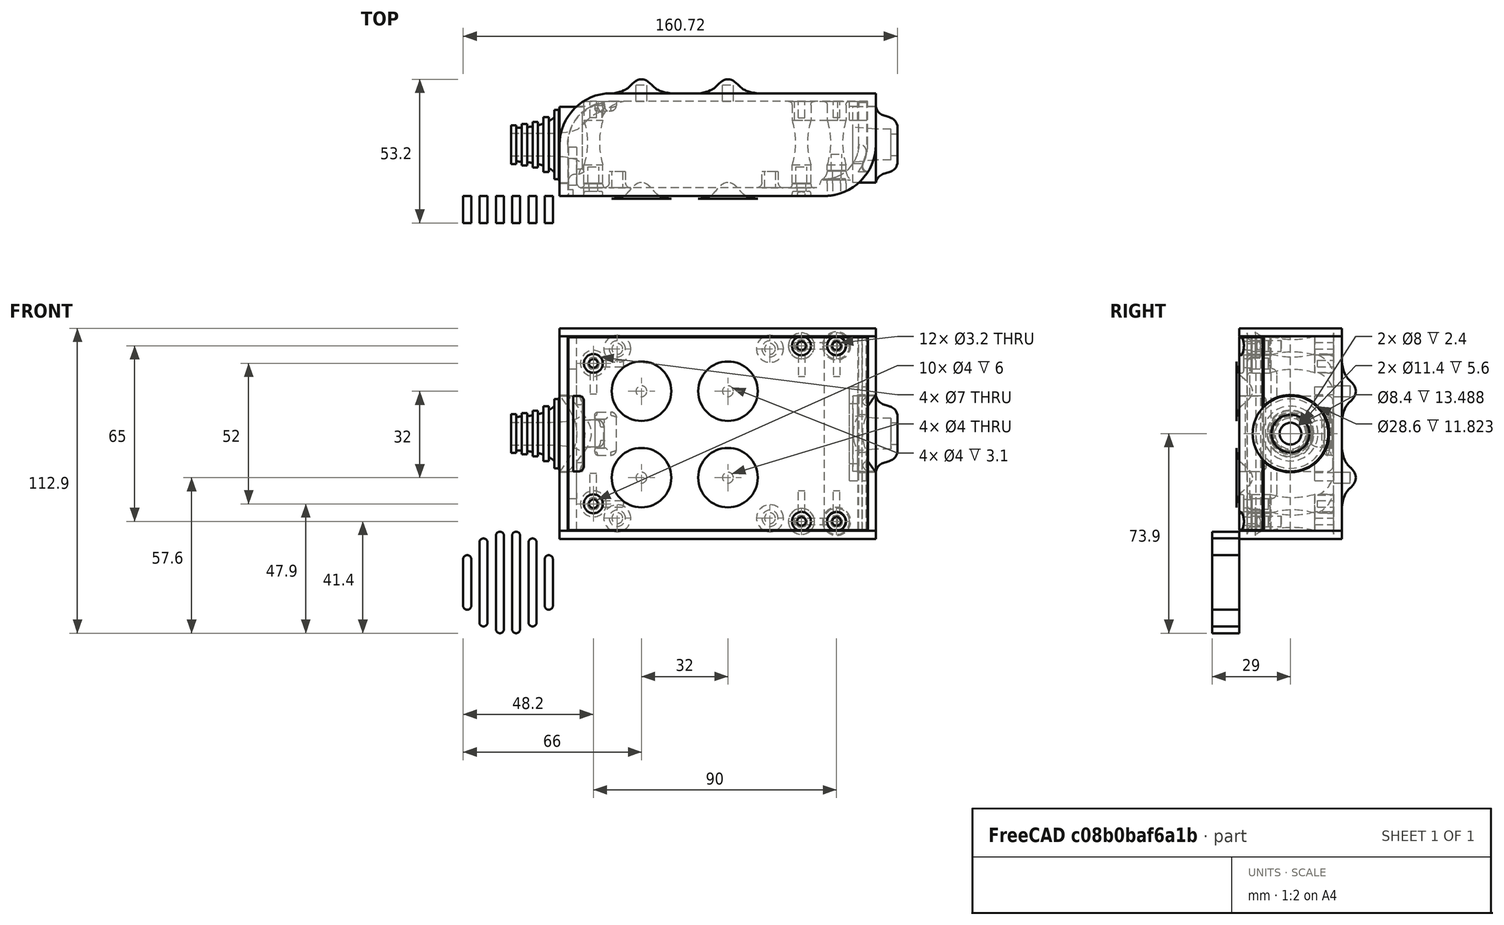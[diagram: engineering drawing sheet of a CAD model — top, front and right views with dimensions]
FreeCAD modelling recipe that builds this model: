
FCSTD DOCUMENT  (FreeCAD 0.19R0.19.2)
Label: enclosure_096
License: All rights reserved
LicenseURL: http://en.wikipedia.org/wiki/All_rights_reserved
objects: Part::Feature×72, Part::Revolution×72, Part::MultiFuse×52, Sketcher::SketchObject×29, Part::Fillet×22, Part::Cylinder×22, Part::Extrusion×19, Part::Cut×19, Part::Box×12, App::MeasureDistance×3
note: 319 computed .brp shape members not serialized (recipe doc carries the construction recipe); baked Part::Feature solids carry a one-line shape summary decoded from their .brp

FEATURE [Sketcher::SketchObject] Sketch  label="topSketch"
  FullyConstrained = true
  sketch-geometry (13):
    g0: LineSegment StartX=117 StartY=19 StartZ=0 EndX=117 EndY=38 EndZ=0
    g1: ArcOfCircle CenterX=98 CenterY=19 CenterZ=0 NormalX=0 NormalY=0 NormalZ=1 AngleXU=0 Radius=19 StartAngle=5.7297 EndAngle=6.28319
    g2: LineSegment StartX=0 StartY=3 StartZ=0 EndX=0 EndY=19 EndZ=0
    g3: LineSegment StartX=19 StartY=38 StartZ=0 EndX=117 EndY=38 EndZ=0
    g4: ArcOfCircle CenterX=19 CenterY=19 CenterZ=0 NormalX=0 NormalY=0 NormalZ=1 AngleXU=0 Radius=19 StartAngle=1.5708 EndAngle=3.14159
    g5: ArcOfCircle CenterX=19 CenterY=19 CenterZ=0 NormalX=0 NormalY=0 NormalZ=1 AngleXU=0 Radius=16 StartAngle=1.5708 EndAngle=3.14159
    g6: ArcOfCircle CenterX=98 CenterY=19 CenterZ=0 NormalX=0 NormalY=0 NormalZ=1 AngleXU=0 Radius=16 StartAngle=5.60905 EndAngle=6.28319
    g7: LineSegment StartX=114 StartY=19 StartZ=0 EndX=114 EndY=35 EndZ=0
    g8: LineSegment StartX=110.5 StartY=9.01251 StartZ=0 EndX=114.163 EndY=9.01251 EndZ=0
    g9: LineSegment StartX=114 StartY=35 StartZ=0 EndX=19 EndY=35 EndZ=0
    g10: LineSegment StartX=0 StartY=3 StartZ=0 EndX=0 EndY=0 EndZ=0
    g11: LineSegment StartX=3 StartY=0 StartZ=0 EndX=0 EndY=0 EndZ=0
    g12: LineSegment StartX=3 StartY=19 StartZ=0 EndX=3 EndY=0 EndZ=0
  constraints (33):
    c: Vertical(g0)
    c: Distance(g0) = 19
    c: Block(g0)
    c: Coincident(g1,g0)
    c: Block(g1)
    c: Vertical(g2)
    c: Block(g2)
    c: Coincident(g3,g0)
    c: Horizontal(g3)
    c: Distance(g3) = 98
    c: Coincident(g4,g3)
    c: Coincident(g4,g2)
    c: Block(g4)
    c: Coincident(g5,g4)
    c: Coincident(g6,g1)
    c: Block(g6)
    c: Block(g5)
    c: Coincident(g7,g6)
    c: Vertical(g7)
    c: Coincident(g8,g6)
    c: Coincident(g8,g1)
    c: Coincident(g9,g7)
    c: Coincident(g9,g5)
    c: Horizontal(g9)
    c: Tangent(g9,g5)
    c: Coincident(g10,g2)
    c: Distance(g10) = 3
    c: Vertical(g10)
    c: Coincident(g11,g10)
    c: Horizontal(g11)
    c: Coincident(g12,g5)
    c: Coincident(g12,g11)
    c: Vertical(g12)
FEATURE [Sketcher::SketchObject] Sketch001  label="bottomSketch"
  FullyConstrained = true
  sketch-geometry (32):
    g0: LineSegment StartX=3.3 StartY=-6.03275e-07 StartZ=0 EndX=98 EndY=-6.03275e-07 EndZ=0
    g1: ArcOfCircle CenterX=98 CenterY=19 CenterZ=0 NormalX=0 NormalY=0 NormalZ=1 AngleXU=0 Radius=19 StartAngle=4.71239 EndAngle=5.71103
    g2: LineSegment StartX=6.3 StartY=8 StartZ=0 EndX=3.3 EndY=8 EndZ=0
    g3: LineSegment StartX=3.3 StartY=8 StartZ=0 EndX=3.3 EndY=-6.03275e-07 EndZ=0
    g4: ArcOfCircle CenterX=8.3 CenterY=5 CenterZ=0 NormalX=0 NormalY=0 NormalZ=1 AngleXU=0 Radius=2 StartAngle=3.14159 EndAngle=4.71239
    g5: LineSegment StartX=6.3 StartY=8 StartZ=0 EndX=6.3 EndY=5 EndZ=0
    g6: ArcOfCircle CenterX=98 CenterY=19 CenterZ=0 NormalX=0 NormalY=0 NormalZ=1 AngleXU=0 Radius=12.7 StartAngle=4.71239 EndAngle=6.28319
    g7: LineSegment StartX=94.7 StartY=3 StartZ=0 EndX=8.3 EndY=3 EndZ=0
    g8-g12: Circle x5 (B-spline internal-alignment scaffolding for g13; pole/knot coordinates omitted)
    g13: BSplineCurve PolesCount=5 KnotsCount=3 Degree=3 IsPeriodic=0
    g14: GeomPoint X=98 Y=6.3 Z=0
    g15: GeomPoint X=96.3938 Y=4.71946 Z=0
    g16: GeomPoint X=94.7 Y=3 Z=0
    g17-g23: Circle x7 (B-spline internal-alignment scaffolding for g24; pole/knot coordinates omitted)
    g24: BSplineCurve PolesCount=7 KnotsCount=5 Degree=3 IsPeriodic=0
    g25-g29: GeomPoint x5 (B-spline internal-alignment scaffolding for g24; pole/knot coordinates omitted)
    g30: ArcOfCircle CenterX=98 CenterY=19 CenterZ=0 NormalX=0 NormalY=0 NormalZ=1 AngleXU=0 Radius=15.7 StartAngle=5.81226 EndAngle=6.28319
    g31: LineSegment StartX=110.7 StartY=19 StartZ=0 EndX=113.7 EndY=19 EndZ=0
  constraints (41):
    c: Horizontal(g0)
    c: Coincident(g1,g0)
    c: Block(g1)
    c: Horizontal(g2)
    c: Distance(g2) = 3
    c: Coincident(g3,g2)
    c: Vertical(g3)
    c: Coincident(g3,g0)
    c: Block(g4)
    c: Block(g2)
    c: Coincident(g5,g2)
    c: Coincident(g5,g4)
    c: Vertical(g5)
    c: Coincident(g6,g1)
    c: Block(g6)
    c: Coincident(g7,g4)
    c: Horizontal(g7)
    c: Block(g0)
    c: Block(g7)
    c: Block(g3)
    c: Coincident(g13,g6)
    c: Weight(g8) = 1
    c: Equal(g8, g9-g12) x4
    c: Coincident(g13,g7)
    c: InternalAlignment(g8-g12 -> g13) x5
    c: InternalAlignment(g14,g13)
    c: InternalAlignment(g15,g13)
    c: InternalAlignment(g16,g13)
    c: Block(g13)
    c: Weight(g17) = 1
    c: Equal(g17, g18-g23) x6
    c: Coincident(g24,g1)
    c: InternalAlignment(g17-g23 -> g24) x7
    c: InternalAlignment(g25-g29 -> g24) x5
    c: Block(g24)
    c: Coincident(g30,g24)
    c: Coincident(g31,g6)
    c: Coincident(g31,g30)
    c: Horizontal(g31)
    c: Block(g31)
    c: Block(g30)
FEATURE [Part::Extrusion] Extrude  label="top"
  Base = -> Sketch
  Dir = (0,0,1)
  DirMode = 2
  FaceMakerClass = Part::FaceMakerBullseye
  LengthFwd = 72
  LengthRev = 0
  Solid = true
  Symmetric = false
FEATURE [Part::Extrusion] Extrude001  label="bottom"
  Base = -> Sketch001
  Dir = (0,0,1)
  DirMode = 2
  FaceMakerClass = Part::FaceMakerBullseye
  LengthFwd = 71.4
  LengthRev = 0
  Placement = pos=(0,0,0.3) rot=(0,0,1;0rad)
  Solid = true
  Symmetric = false
FEATURE [Sketcher::SketchObject] Sketch002  label="topSketch001"
  FullyConstrained = true
  sketch-geometry (6):
    g0: LineSegment StartX=19 StartY=38 StartZ=0 EndX=117 EndY=38 EndZ=0
    g1: ArcOfCircle CenterX=19 CenterY=19 CenterZ=0 NormalX=0 NormalY=0 NormalZ=1 AngleXU=0 Radius=19 StartAngle=1.5708 EndAngle=3.14159
    g2: LineSegment StartX=117 StartY=38 StartZ=0 EndX=117 EndY=19 EndZ=0
    g3: LineSegment StartX=98 StartY=1.0161e-12 StartZ=0 EndX=5.22862e-06 EndY=1.0161e-12 EndZ=0
    g4: LineSegment StartX=5.22862e-06 StartY=19 StartZ=0 EndX=5.22862e-06 EndY=1.0161e-12 EndZ=0
    g5: ArcOfCircle CenterX=98 CenterY=19 CenterZ=0 NormalX=0 NormalY=0 NormalZ=1 AngleXU=0 Radius=19 StartAngle=4.71239 EndAngle=6.28319
  constraints (16):
    c: Horizontal(g0)
    c: Distance(g0) = 98
    c: Coincident(g1,g0)
    c: Block(g1)
    c: Coincident(g2,g0)
    c: Vertical(g2)
    c: Distance(g2) = 19
    c: Horizontal(g3)
    c: Coincident(g4,g1)
    c: Vertical(g4)
    c: Coincident(g3,g4)
    c: Block(g3)
    c: Coincident(g5,g2)
    c: Coincident(g5,g3)
    c: Block(g0)
    c: Block(g5)
FEATURE [Part::Extrusion] Extrude002  label="sideA"
  Base = -> Sketch002
  Dir = (0,0,1)
  DirMode = 2
  FaceMakerClass = Part::FaceMakerBullseye
  LengthFwd = 3
  LengthRev = 0
  Placement = pos=(0,0,-3) rot=(0,0,1;0rad)
  Solid = true
  Symmetric = false
FEATURE [Sketcher::SketchObject] Sketch003  label="topSketch002"
  FullyConstrained = true
  sketch-geometry (6):
    g0: LineSegment StartX=19 StartY=38 StartZ=0 EndX=117 EndY=38 EndZ=0
    g1: ArcOfCircle CenterX=19 CenterY=19 CenterZ=0 NormalX=0 NormalY=0 NormalZ=1 AngleXU=0 Radius=19 StartAngle=1.5708 EndAngle=3.14159
    g2: LineSegment StartX=117 StartY=38 StartZ=0 EndX=117 EndY=19 EndZ=0
    g3: LineSegment StartX=98 StartY=1.0161e-12 StartZ=0 EndX=5.22862e-06 EndY=1.0161e-12 EndZ=0
    g4: LineSegment StartX=5.22862e-06 StartY=19 StartZ=0 EndX=5.22862e-06 EndY=1.0161e-12 EndZ=0
    g5: ArcOfCircle CenterX=98 CenterY=19 CenterZ=0 NormalX=0 NormalY=0 NormalZ=1 AngleXU=0 Radius=19 StartAngle=4.71239 EndAngle=6.28319
  constraints (16):
    c: Horizontal(g0)
    c: Distance(g0) = 98
    c: Coincident(g1,g0)
    c: Block(g1)
    c: Coincident(g2,g0)
    c: Vertical(g2)
    c: Distance(g2) = 19
    c: Horizontal(g3)
    c: Coincident(g4,g1)
    c: Vertical(g4)
    c: Coincident(g3,g4)
    c: Block(g3)
    c: Coincident(g5,g2)
    c: Coincident(g5,g3)
    c: Block(g0)
    c: Block(g5)
FEATURE [Part::Extrusion] Extrude003  label="sideB"
  Base = -> Sketch003
  Dir = (0,0,1)
  DirMode = 2
  FaceMakerClass = Part::FaceMakerBullseye
  LengthFwd = 3
  LengthRev = 0
  Placement = pos=(0,0,72) rot=(0,0,1;0rad)
  Solid = true
  Symmetric = false
FEATURE [Sketcher::SketchObject] Sketch004
  FullyConstrained = true
  MapMode = 3
  Placement = pos=(0,0,0) rot=(1,0,0;1.5708rad)
  Support = -> [Extrude]
  sketch-geometry (8):
    g0: Circle CenterX=80.351 CenterY=-67.6202 CenterZ=0 NormalX=0 NormalY=0 NormalZ=1 AngleXU=0 Radius=2
    g1: Circle CenterX=80.351 CenterY=-67.6202 CenterZ=0 NormalX=0 NormalY=0 NormalZ=1 AngleXU=0 Radius=3
    g2: Circle CenterX=80.351 CenterY=-4.92017 CenterZ=0 NormalX=0 NormalY=0 NormalZ=1 AngleXU=0 Radius=2
    g3: Circle CenterX=80.351 CenterY=-4.92017 CenterZ=0 NormalX=0 NormalY=0 NormalZ=1 AngleXU=0 Radius=3
    g4: Circle CenterX=23.851 CenterY=-4.92017 CenterZ=0 NormalX=0 NormalY=0 NormalZ=1 AngleXU=0 Radius=2
    g5: Circle CenterX=23.851 CenterY=-4.92017 CenterZ=0 NormalX=0 NormalY=0 NormalZ=1 AngleXU=0 Radius=3
    g6: Circle CenterX=23.851 CenterY=-67.6202 CenterZ=0 NormalX=0 NormalY=0 NormalZ=1 AngleXU=0 Radius=2
    g7: Circle CenterX=23.851 CenterY=-67.6202 CenterZ=0 NormalX=0 NormalY=0 NormalZ=1 AngleXU=0 Radius=3
  constraints (8):
    c: Block(g3)
    c: Block(g2)
    c: Block(g1)
    c: Block(g0)
    c: Block(g6)
    c: Block(g7)
    c: Block(g4)
    c: Block(g5)
FEATURE [Part::Extrusion] Extrude004
  Base = -> Sketch004
  Dir = (0,-1,2e-16)
  DirMode = 2
  FaceMakerClass = Part::FaceMakerBullseye
  LengthFwd = 6
  LengthRev = 0
  Placement = pos=(0,9,0) rot=(0,0,1;0rad)
  Solid = true
  Symmetric = false
FEATURE [Sketcher::SketchObject] Sketch005
  FullyConstrained = true
  MapMode = 3
  Placement = pos=(0,0,0) rot=(1,0,0;1.5708rad)
  Support = -> [Extrude]
  sketch-geometry (8):
    g0: Circle CenterX=80.351 CenterY=-67.6202 CenterZ=0 NormalX=0 NormalY=0 NormalZ=1 AngleXU=0 Radius=3
    g1: Circle CenterX=80.351 CenterY=-4.92017 CenterZ=0 NormalX=0 NormalY=0 NormalZ=1 AngleXU=0 Radius=3
    g2: Circle CenterX=23.851 CenterY=-4.92017 CenterZ=0 NormalX=0 NormalY=0 NormalZ=1 AngleXU=0 Radius=3
    g3: Circle CenterX=23.851 CenterY=-67.6202 CenterZ=0 NormalX=0 NormalY=0 NormalZ=1 AngleXU=0 Radius=3
    g4: Circle CenterX=23.851 CenterY=-67.6202 CenterZ=0 NormalX=0 NormalY=0 NormalZ=1 AngleXU=0 Radius=5
    g5: Circle CenterX=80.351 CenterY=-67.6202 CenterZ=0 NormalX=0 NormalY=0 NormalZ=1 AngleXU=0 Radius=5
    g6: Circle CenterX=23.851 CenterY=-4.92017 CenterZ=0 NormalX=0 NormalY=0 NormalZ=1 AngleXU=0 Radius=5
    g7: Circle CenterX=80.351 CenterY=-4.92017 CenterZ=0 NormalX=0 NormalY=0 NormalZ=1 AngleXU=0 Radius=5
  constraints (8):
    c: Block(g1)
    c: Block(g0)
    c: Block(g3)
    c: Block(g2)
    c: Block(g5)
    c: Block(g4)
    c: Block(g6)
    c: Block(g7)
FEATURE [Part::Extrusion] Extrude005
  Base = -> Sketch005
  Dir = (0,-1,2e-16)
  DirMode = 2
  FaceMakerClass = Part::FaceMakerBullseye
  LengthFwd = 2
  LengthRev = 0
  Solid = true
  Symmetric = false
FEATURE [Sketcher::SketchObject] Sketch006
  FullyConstrained = true
  MapMode = 3
  Placement = pos=(0,0,0) rot=(1,0,0;1.5708rad)
  sketch-geometry (8):
    g0: Circle CenterX=80.351 CenterY=-67.6202 CenterZ=0 NormalX=0 NormalY=0 NormalZ=1 AngleXU=0 Radius=3
    g1: Circle CenterX=80.351 CenterY=-4.92017 CenterZ=0 NormalX=0 NormalY=0 NormalZ=1 AngleXU=0 Radius=3
    g2: Circle CenterX=23.851 CenterY=-4.92017 CenterZ=0 NormalX=0 NormalY=0 NormalZ=1 AngleXU=0 Radius=3
    g3: Circle CenterX=23.851 CenterY=-67.6202 CenterZ=0 NormalX=0 NormalY=0 NormalZ=1 AngleXU=0 Radius=3
    g4: Circle CenterX=23.851 CenterY=-67.6202 CenterZ=0 NormalX=0 NormalY=0 NormalZ=1 AngleXU=0 Radius=5
    g5: Circle CenterX=80.351 CenterY=-67.6202 CenterZ=0 NormalX=0 NormalY=0 NormalZ=1 AngleXU=0 Radius=5
    g6: Circle CenterX=23.851 CenterY=-4.92017 CenterZ=0 NormalX=0 NormalY=0 NormalZ=1 AngleXU=0 Radius=5
    g7: Circle CenterX=80.351 CenterY=-4.92017 CenterZ=0 NormalX=0 NormalY=0 NormalZ=1 AngleXU=0 Radius=5
  constraints (8):
    c: Block(g1)
    c: Block(g0)
    c: Block(g3)
    c: Block(g2)
    c: Block(g5)
    c: Block(g4)
    c: Block(g6)
    c: Block(g7)
FEATURE [Part::Extrusion] Extrude007
  Base = -> Sketch006
  Dir = (0,-1,2e-16)
  DirMode = 2
  FaceMakerClass = Part::FaceMakerBullseye
  LengthFwd = 2
  LengthRev = 0
  Solid = true
  Symmetric = false
FEATURE [Part::Fillet] Fillet
  Base = -> Extrude007
  Edges = 4 edges r=1.99: [Edge6,Edge12,Edge18,Edge24]
FEATURE [Part::Cut] Cut
  Base = -> Extrude005
  Placement = pos=(0,5,0) rot=(0,0,1;0rad)
  Tool = -> Fillet
FEATURE [Part::MultiFuse] Fusion  label="pCBScrews"
  Placement = pos=(-2.5,0,72.3) rot=(0,0,1;0rad)
  Shapes = -> [Extrude004,Cut]
FEATURE [App::MeasureDistance] Distance  label="Distance: 0.69 mm"
  Distance = 0.685967
  P1 = (24.0138,2.9647,0.3)
  P2 = (23.8901,3,-0.373787)
FEATURE [App::MeasureDistance] Distance001  label="Distance: 0.53 mm"
  Distance = 0.533607
  P1 = (80.2939,3,72.2334)
  P2 = (80.281,2.99661,71.7)
FEATURE [Part::Fillet] Fillet001
  Base = -> Extrude001
  Edges = 1 edges r=2.4: [Edge17]
FEATURE [Part::Fillet] Fillet002  label="bottom001"
  Base = -> Fillet001
  Edges = 1 edges r=2.4: [Edge36]
FEATURE [Part::Fillet] Fillet003  label="top001"
  Base = -> Extrude
  Edges = 1 edges r=2: [Edge1]
FEATURE [Sketcher::SketchObject] Sketch007
  FullyConstrained = true
  sketch-geometry (16):
    g0: LineSegment StartX=4 StartY=0 StartZ=0 EndX=4 EndY=2.4 EndZ=0
    g1: LineSegment StartX=4 StartY=2.4 StartZ=0 EndX=7 EndY=2.4 EndZ=0
    g2: LineSegment StartX=4 StartY=0 StartZ=0 EndX=5.7 EndY=0 EndZ=0
    g3: LineSegment StartX=5.7 StartY=0 StartZ=0 EndX=5.7 EndY=-5.6 EndZ=0
    g4-g8: Circle x5 (B-spline internal-alignment scaffolding for g9; pole/knot coordinates omitted)
    g9: BSplineCurve PolesCount=5 KnotsCount=3 Degree=3 IsPeriodic=0
    g10: GeomPoint X=7 Y=2.4 Z=0
    g11: GeomPoint X=10.4582 Y=-1.55472 Z=0
    g12: GeomPoint X=14 Y=-5.6 Z=0
    g13: LineSegment StartX=14 StartY=-5.6 StartZ=0 EndX=14 EndY=-14.1 EndZ=0
    g14: LineSegment StartX=14 StartY=-14.1 StartZ=0 EndX=6.5 EndY=-14.1 EndZ=0
    g15: LineSegment StartX=5.7 StartY=-5.6 StartZ=0 EndX=6.5 EndY=-14.1 EndZ=0
  constraints (28):
    c: Distance(g0) = 2.4
    c: Vertical(g0)
    c: Block(g0)
    c: Coincident(g1,g0)
    c: Horizontal(g1)
    c: Distance(g1) = 3
    c: Coincident(g2,g0)
    c: Horizontal(g2)
    c: Distance(g2) = 1.7
    c: Coincident(g3,g2)
    c: Vertical(g3)
    c: Distance(g3) = 5.6
    c: Coincident(g9,g1)
    c: Weight(g4) = 1
    c: Equal(g4, g5-g8) x4
    c: InternalAlignment(g4-g8 -> g9) x5
    c: InternalAlignment(g10,g9)
    c: InternalAlignment(g11,g9)
    c: InternalAlignment(g12,g9)
    c: Block(g9)
    c: Coincident(g13,g9)
    c: Vertical(g13)
    c: Distance(g13) = 8.5
    c: Coincident(g14,g13)
    c: Horizontal(g14)
    c: Distance(g14) = 7.5
    c: Coincident(g15,g3)
    c: Coincident(g15,g14)
FEATURE [Part::Feature] Face
  shape: bbox 10 x 16.5 x 2e-07 mm, 1 faces, 0 solids (baked)
FEATURE [Part::Revolution] Revolve  label="plugHousing"
  Angle = 360
  Axis = (0,1,0)
  Base = (0,0,0)
  FaceMakerClass = Part::FaceMakerBullseye
  Placement = pos=(0,0,36.15) rot=(0,0,1;0rad)
  Solid = false
  Source = -> Face
  Symmetric = false
FEATURE [Part::Feature] Face001
  shape: bbox 10 x 16.5 x 2e-07 mm, 1 faces, 0 solids (baked)
FEATURE [Part::Revolution] Revolve001  label="plugHousing001"
  Angle = 360
  Axis = (0,1,0)
  Base = (0,0,0)
  FaceMakerClass = Part::FaceMakerBullseye
  Placement = pos=(0,0,36.15) rot=(0,0,1;0rad)
  Solid = false
  Source = -> Face001
  Symmetric = false
FEATURE [Part::MultiFuse] Fusion001  label="plugHousing002"
  Placement = pos=(0,0,0) rot=(0,0,1;1.5708rad)
  Shapes = -> [Revolve001,Revolve]
FEATURE [Part::Feature] Face002
  shape: bbox 10 x 16.5 x 2e-07 mm, 1 faces, 0 solids (baked)
FEATURE [Part::Revolution] Revolve003  label="plugHousing005"
  Angle = 360
  Axis = (0,1,0)
  Base = (0,0,0)
  FaceMakerClass = Part::FaceMakerBullseye
  Placement = pos=(0,0,36.15) rot=(0,0,1;0rad)
  Solid = false
  Source = -> Face002
  Symmetric = false
FEATURE [Part::Feature] Face003
  shape: bbox 10 x 16.5 x 2e-07 mm, 1 faces, 0 solids (baked)
FEATURE [Part::Revolution] Revolve002  label="plugHousing003"
  Angle = 360
  Axis = (0,1,0)
  Base = (0,0,0)
  FaceMakerClass = Part::FaceMakerBullseye
  Placement = pos=(0,0,36.15) rot=(0,0,1;0rad)
  Solid = false
  Source = -> Face003
  Symmetric = false
FEATURE [Part::MultiFuse] Fusion002  label="plugHousing004"
  Placement = pos=(0,0,0) rot=(0,0,1;1.5708rad)
  Shapes = -> [Revolve002,Revolve003]
FEATURE [Part::MultiFuse] Fusion003  label="plugHousing006"
  Placement = pos=(0,19,0) rot=(0,0,1;3.14159rad)
  Shapes = -> [Fusion002,Fusion001]
FEATURE [Part::Feature] Face004
  shape: bbox 10 x 16.5 x 2e-07 mm, 1 faces, 0 solids (baked)
FEATURE [Part::Revolution] Revolve006  label="plugHousing010"
  Angle = 360
  Axis = (0,1,0)
  Base = (0,0,0)
  FaceMakerClass = Part::FaceMakerBullseye
  Placement = pos=(0,0,36.15) rot=(0,0,1;0rad)
  Solid = false
  Source = -> Face004
  Symmetric = false
FEATURE [Part::Feature] Face005
  shape: bbox 10 x 16.5 x 2e-07 mm, 1 faces, 0 solids (baked)
FEATURE [Part::Revolution] Revolve007  label="plugHousing011"
  Angle = 360
  Axis = (0,1,0)
  Base = (0,0,0)
  FaceMakerClass = Part::FaceMakerBullseye
  Placement = pos=(0,0,36.15) rot=(0,0,1;0rad)
  Solid = false
  Source = -> Face005
  Symmetric = false
FEATURE [Part::Feature] Face006
  shape: bbox 10 x 16.5 x 2e-07 mm, 1 faces, 0 solids (baked)
FEATURE [Part::Revolution] Revolve004  label="plugHousing007"
  Angle = 360
  Axis = (0,1,0)
  Base = (0,0,0)
  FaceMakerClass = Part::FaceMakerBullseye
  Placement = pos=(0,0,36.15) rot=(0,0,1;0rad)
  Solid = false
  Source = -> Face006
  Symmetric = false
FEATURE [Part::MultiFuse] Fusion004  label="plugHousing009"
  Placement = pos=(0,0,0) rot=(0,0,1;1.5708rad)
  Shapes = -> [Revolve004,Revolve007]
FEATURE [Part::Feature] Face007
  shape: bbox 10 x 16.5 x 2e-07 mm, 1 faces, 0 solids (baked)
FEATURE [Part::Revolution] Revolve005  label="plugHousing008"
  Angle = 360
  Axis = (0,1,0)
  Base = (0,0,0)
  FaceMakerClass = Part::FaceMakerBullseye
  Placement = pos=(0,0,36.15) rot=(0,0,1;0rad)
  Solid = false
  Source = -> Face007
  Symmetric = false
FEATURE [Part::MultiFuse] Fusion005  label="plugHousing012"
  Placement = pos=(0,0,0) rot=(0,0,1;1.5708rad)
  Shapes = -> [Revolve006,Revolve005]
FEATURE [Part::MultiFuse] Fusion006  label="plugHousing013"
  Placement = pos=(0,19,0) rot=(0,0,1;3.14159rad)
  Shapes = -> [Fusion005,Fusion004]
FEATURE [Part::MultiFuse] Fusion007  label="plugHousing014"
  Placement = pos=(122.621,0,-0.15) rot=(0,0,1;0rad)
  Shapes = -> [Fusion003,Fusion006]
FEATURE [Part::Cylinder] Cylinder002
  Angle = 360
  AttacherType = Attacher::AttachEngine3D
  Height = 20
  Placement = pos=(0,0,36.15) rot=(0,0,1;0rad)
  Radius = 4
FEATURE [Part::Cylinder] Cylinder003
  Angle = 360
  AttacherType = Attacher::AttachEngine3D
  Height = 10
  Placement = pos=(0,0,36.15) rot=(0,0,1;0rad)
  Radius = 4
FEATURE [Part::MultiFuse] Fusion009  label="removeToCreateHoleForPlugHousing"
  Placement = pos=(70,19,36.15) rot=(0,1,0;1.5708rad)
  Shapes = -> [Cylinder002,Cylinder003]
FEATURE [Part::Cylinder] Cylinder004
  Angle = 360
  AttacherType = Attacher::AttachEngine3D
  Height = 20
  Placement = pos=(0,0,36.15) rot=(0,0,1;0rad)
  Radius = 4
FEATURE [Part::Cylinder] Cylinder005
  Angle = 360
  AttacherType = Attacher::AttachEngine3D
  Height = 10
  Placement = pos=(0,0,36.15) rot=(0,0,1;0rad)
  Radius = 4
FEATURE [Part::MultiFuse] Fusion010  label="removeToCreateHoleForPlugHousing001"
  Placement = pos=(70,19,36.15) rot=(0,1,0;1.5708rad)
  Shapes = -> [Cylinder004,Cylinder005]
FEATURE [Part::Cut] Cut001
  Base = -> Fillet003
  Tool = -> Fusion010
FEATURE [Part::Cut] Cut002  label="Bottom"
  Base = -> Fillet002
  Tool = -> Fusion009
FEATURE [Part::Feature] Face008
  shape: bbox 10 x 16.5 x 2e-07 mm, 1 faces, 0 solids (baked)
FEATURE [Part::Revolution] Revolve011  label="plugHousing021"
  Angle = 360
  Axis = (0,1,0)
  Base = (0,0,0)
  FaceMakerClass = Part::FaceMakerBullseye
  Placement = pos=(0,0,36.15) rot=(0,0,1;0rad)
  Solid = false
  Source = -> Face008
  Symmetric = false
FEATURE [Part::Feature] Face009
  shape: bbox 10 x 16.5 x 2e-07 mm, 1 faces, 0 solids (baked)
FEATURE [Part::Revolution] Revolve012  label="plugHousing022"
  Angle = 360
  Axis = (0,1,0)
  Base = (0,0,0)
  FaceMakerClass = Part::FaceMakerBullseye
  Placement = pos=(0,0,36.15) rot=(0,0,1;0rad)
  Solid = false
  Source = -> Face009
  Symmetric = false
FEATURE [Part::Feature] Face010 .. Face013  x4 (patterned run collapsed; names and placements below)
  shape: bbox 10 x 16.5 x 2e-07 mm, 1 faces, 0 solids (baked)
FEATURE [Part::Revolution] Revolve015  label="plugHousing027"
  Angle = 360
  Axis = (0,1,0)
  Base = (0,0,0)
  FaceMakerClass = Part::FaceMakerBullseye
  Placement = pos=(0,0,36.15) rot=(0,0,1;0rad)
  Solid = false
  Source = -> Face013
  Symmetric = false
FEATURE [Part::Feature] Face014
  shape: bbox 10 x 16.5 x 2e-07 mm, 1 faces, 0 solids (baked)
FEATURE [Part::Feature] Face015
  shape: bbox 10 x 16.5 x 2e-07 mm, 1 faces, 0 solids (baked)
FEATURE [Part::Feature] Face016
  shape: bbox 10 x 16.5 x 2e-07 mm, 1 faces, 0 solids (baked)
FEATURE [Part::Revolution] Revolve019  label="plugHousing033"
  Angle = 360
  Axis = (0,1,0)
  Base = (0,0,0)
  FaceMakerClass = Part::FaceMakerBullseye
  Placement = pos=(0,0,36.15) rot=(0,0,1;0rad)
  Solid = false
  Source = -> Face016
  Symmetric = false
FEATURE [Part::Feature] Face017
  shape: bbox 10 x 16.5 x 2e-07 mm, 1 faces, 0 solids (baked)
FEATURE [Part::Revolution] Revolve020  label="plugHousing034"
  Angle = 360
  Axis = (0,1,0)
  Base = (0,0,0)
  FaceMakerClass = Part::FaceMakerBullseye
  Placement = pos=(0,0,36.15) rot=(0,0,1;0rad)
  Solid = false
  Source = -> Face017
  Symmetric = false
FEATURE [Part::Feature] Face018
  shape: bbox 10 x 16.5 x 2e-07 mm, 1 faces, 0 solids (baked)
FEATURE [Part::Revolution] Revolve016  label="plugHousing030"
  Angle = 360
  Axis = (0,1,0)
  Base = (0,0,0)
  FaceMakerClass = Part::FaceMakerBullseye
  Placement = pos=(0,0,36.15) rot=(0,0,1;0rad)
  Solid = false
  Source = -> Face018
  Symmetric = false
FEATURE [Part::MultiFuse] Fusion020  label="plugHousing038"
  Placement = pos=(0,0,0) rot=(0,0,1;1.5708rad)
  Shapes = -> [Revolve016,Revolve020]
FEATURE [Part::Feature] Face019
  shape: bbox 10 x 16.5 x 2e-07 mm, 1 faces, 0 solids (baked)
FEATURE [Part::Feature] Face020
  shape: bbox 10 x 16.5 x 2e-07 mm, 1 faces, 0 solids (baked)
FEATURE [Part::Revolution] Revolve017  label="plugHousing031"
  Angle = 360
  Axis = (0,1,0)
  Base = (0,0,0)
  FaceMakerClass = Part::FaceMakerBullseye
  Placement = pos=(0,0,36.15) rot=(0,0,1;0rad)
  Solid = false
  Source = -> Face020
  Symmetric = false
FEATURE [Part::MultiFuse] Fusion021  label="plugHousing039"
  Placement = pos=(0,0,0) rot=(0,0,1;1.5708rad)
  Shapes = -> [Revolve019,Revolve017]
FEATURE [Part::MultiFuse] Fusion023  label="plugHousing041"
  Placement = pos=(0,19,0) rot=(0,0,1;3.14159rad)
  Shapes = -> [Fusion021,Fusion020]
FEATURE [Part::Revolution] Revolve022  label="plugHousing043"
  Angle = 360
  Axis = (0,1,0)
  Base = (0,0,0)
  FaceMakerClass = Part::FaceMakerBullseye
  Placement = pos=(0,0,36.15) rot=(0,0,1;0rad)
  Solid = false
  Source = -> Face019
  Symmetric = false
FEATURE [Part::Feature] Face021
  shape: bbox 10 x 16.5 x 2e-07 mm, 1 faces, 0 solids (baked)
FEATURE [Part::Revolution] Revolve023  label="plugHousing044"
  Angle = 360
  Axis = (0,1,0)
  Base = (0,0,0)
  FaceMakerClass = Part::FaceMakerBullseye
  Placement = pos=(0,0,36.15) rot=(0,0,1;0rad)
  Solid = false
  Source = -> Face021
  Symmetric = false
FEATURE [Part::Feature] Face022
  shape: bbox 10 x 16.5 x 2e-07 mm, 1 faces, 0 solids (baked)
FEATURE [Part::Revolution] Revolve018  label="plugHousing032"
  Angle = 360
  Axis = (0,1,0)
  Base = (0,0,0)
  FaceMakerClass = Part::FaceMakerBullseye
  Placement = pos=(0,0,36.15) rot=(0,0,1;0rad)
  Solid = false
  Source = -> Face022
  Symmetric = false
FEATURE [Part::MultiFuse] Fusion022  label="plugHousing040"
  Placement = pos=(0,0,0) rot=(0,0,1;1.5708rad)
  Shapes = -> [Revolve018,Revolve023]
FEATURE [Part::Feature] Face023
  shape: bbox 10 x 16.5 x 2e-07 mm, 1 faces, 0 solids (baked)
FEATURE [Part::Revolution] Revolve021  label="plugHousing035"
  Angle = 360
  Axis = (0,1,0)
  Base = (0,0,0)
  FaceMakerClass = Part::FaceMakerBullseye
  Placement = pos=(0,0,36.15) rot=(0,0,1;0rad)
  Solid = false
  Source = -> Face023
  Symmetric = false
FEATURE [Part::MultiFuse] Fusion018  label="plugHousing036"
  Placement = pos=(0,0,0) rot=(0,0,1;1.5708rad)
  Shapes = -> [Revolve022,Revolve021]
FEATURE [Part::MultiFuse] Fusion019  label="plugHousing037"
  Placement = pos=(0,19,0) rot=(0,0,1;3.14159rad)
  Shapes = -> [Fusion018,Fusion022]
FEATURE [Part::MultiFuse] Fusion024  label="plugHousing042"
  Placement = pos=(122.621,0,-0.15) rot=(0,0,1;0rad)
  Shapes = -> [Fusion023,Fusion019]
FEATURE [Part::Cylinder] Cylinder006
  Angle = 360
  AttacherType = Attacher::AttachEngine3D
  Height = 20
  Placement = pos=(0,0,36.15) rot=(0,0,1;0rad)
  Radius = 14.3
FEATURE [Part::Cylinder] Cylinder007
  Angle = 360
  AttacherType = Attacher::AttachEngine3D
  Height = 10
  Placement = pos=(0,0,36.15) rot=(0,0,1;0rad)
  Radius = 4
FEATURE [Part::MultiFuse] Fusion026  label="removeToCreteHoleForPlugHousing"
  Placement = pos=(70,19,36) rot=(0,1,0;1.5708rad)
  Shapes = -> [Cylinder006,Cylinder007]
FEATURE [Part::Box] Box001  label="Cube001"
  AttacherType = Attacher::AttachEngine3D
  Height = 28
  Length = 3
  Placement = pos=(110.7,19,22) rot=(0,0,1;0rad)
  Width = 15.7
FEATURE [Part::Cut] Cut003  label="top002"
  Base = -> Cut001
  Tool = -> Fusion007
FEATURE [Part::Revolution] Revolve008  label="plugHousing015"
  Angle = 360
  Axis = (0,1,0)
  Base = (0,0,0)
  FaceMakerClass = Part::FaceMakerBullseye
  Placement = pos=(0,0,36.15) rot=(0,0,1;0rad)
  Solid = false
  Source = -> Face010
  Symmetric = false
FEATURE [Part::MultiFuse] Fusion013  label="plugHousing020"
  Placement = pos=(0,0,0) rot=(0,0,1;1.5708rad)
  Shapes = -> [Revolve008,Revolve012]
FEATURE [Part::Cut] Cut004  label="top003"
  Base = -> Cut003
  Placement = pos=(1,0,0) rot=(0,0,1;0rad)
  Tool = -> Fusion026
FEATURE [Part::Cylinder] Cylinder008
  Angle = 360
  AttacherType = Attacher::AttachEngine3D
  Height = 20
  Placement = pos=(0,0,36.15) rot=(0,0,1;0rad)
  Radius = 10.3
FEATURE [Part::Cylinder] Cylinder009
  Angle = 360
  AttacherType = Attacher::AttachEngine3D
  Height = 10
  Placement = pos=(0,0,36.15) rot=(0,0,1;0rad)
  Radius = 4
FEATURE [Part::MultiFuse] Fusion027  label="removeToCreteHoleForPlugHousing001"
  Placement = pos=(70,19,36) rot=(0,1,0;1.5708rad)
  Shapes = -> [Cylinder008,Cylinder009]
FEATURE [Part::Cut] Cut005  label="plugHousingTab"
  Base = -> Box001
  Tool = -> Fusion027
FEATURE [Part::MultiFuse] Fusion028  label="plugHousing045"
  Shapes = -> [Fusion024,Cut005]
FEATURE [Part::Box] Box002  label="Cube002"
  AttacherType = Attacher::AttachEngine3D
  Height = 28.8
  Length = 3
  Placement = pos=(107.3,28,21.6) rot=(0,0,1;0rad)
  Width = 7
FEATURE [Part::Box] Box003  label="Cube003"
  AttacherType = Attacher::AttachEngine3D
  Height = 3
  Length = 6.4
  Placement = pos=(107.3,28,18.6) rot=(0,0,1;0rad)
  Width = 7
FEATURE [Part::Box] Box004  label="Cube004"
  AttacherType = Attacher::AttachEngine3D
  Height = 3
  Length = 6.4
  Placement = pos=(107.3,28,50.4) rot=(0,0,1;0rad)
  Width = 7
FEATURE [Part::MultiFuse] Fusion029  label="plugHousingBracketHolder"
  Shapes = -> [Box004,Box002,Box003]
FEATURE [Part::Cylinder] Cylinder010
  Angle = 360
  AttacherType = Attacher::AttachEngine3D
  Height = 20
  Placement = pos=(0,0,36.15) rot=(0,0,1;0rad)
  Radius = 14.3
FEATURE [Part::Cylinder] Cylinder011
  Angle = 360
  AttacherType = Attacher::AttachEngine3D
  Height = 10
  Placement = pos=(0,0,36.15) rot=(0,0,1;0rad)
  Radius = 4
FEATURE [Part::MultiFuse] Fusion030  label="removeToCreteHoleForPlugHousing002"
  Placement = pos=(70,19,36) rot=(0,1,0;1.5708rad)
  Shapes = -> [Cylinder010,Cylinder011]
FEATURE [Part::Cut] Cut006  label="plugHousingBracketHolder001"
  Base = -> Fusion029
  Tool = -> Fusion030
FEATURE [Part::Cylinder] Cylinder012
  Angle = 360
  AttacherType = Attacher::AttachEngine3D
  Height = 20
  Placement = pos=(0,0,36.15) rot=(0,0,1;0rad)
  Radius = 7
FEATURE [Part::Cylinder] Cylinder013
  Angle = 360
  AttacherType = Attacher::AttachEngine3D
  Height = 10
  Placement = pos=(0,0,36.15) rot=(0,0,1;0rad)
  Radius = 4
FEATURE [Part::MultiFuse] Fusion032  label="removeToCreteHoleForPlugHousing003"
  Placement = pos=(70,19,36) rot=(0,1,0;1.5708rad)
  Shapes = -> [Cylinder012,Cylinder013]
FEATURE [Part::Cut] Cut007  label="bottom002"
  Base = -> Cut002
  Tool = -> Fusion032
FEATURE [Sketcher::SketchObject] Sketch008
  FullyConstrained = true
  sketch-geometry (54):
    g0: LineSegment StartX=-4.2 StartY=0 StartZ=0 EndX=-6.2 EndY=0 EndZ=0
    g1: LineSegment StartX=-14 StartY=-18 StartZ=0 EndX=-14 EndY=-26.5 EndZ=0
    g2: LineSegment StartX=-4.2 StartY=0 StartZ=0 EndX=-4.2 EndY=-13.4877 EndZ=0
    g3: Circle CenterX=-4.2 CenterY=-13.4877 CenterZ=0 NormalX=0 NormalY=0 NormalZ=1 AngleXU=0 Radius=1
    g4: Circle CenterX=-4.2 CenterY=-26.5 CenterZ=0 NormalX=0 NormalY=0 NormalZ=1 AngleXU=0 Radius=1
    g5: Circle CenterX=-8.2 CenterY=-26.5 CenterZ=0 NormalX=0 NormalY=0 NormalZ=1 AngleXU=0 Radius=1
    g6: BSplineCurve PolesCount=3 KnotsCount=2 Degree=2 IsPeriodic=0
    g7: GeomPoint X=-4.2 Y=-13.4877 Z=0
    g8: GeomPoint X=-8.2 Y=-26.5 Z=0
    g9: LineSegment StartX=-14 StartY=-26.5 StartZ=0 EndX=-8.2 EndY=-26.5 EndZ=0
    g10: LineSegment StartX=-10.15 StartY=-12 StartZ=0 EndX=-10.15 EndY=-14 EndZ=0
    g11: LineSegment StartX=-12.8401 StartY=-16 StartZ=0 EndX=-10.1571 EndY=-16 EndZ=0
    g12: LineSegment StartX=-10.15 StartY=-14 StartZ=0 EndX=-8.70761 EndY=-14 EndZ=0
    g13: LineSegment StartX=-12.8401 StartY=-16 StartZ=0 EndX=-12.8401 EndY=-17.6958 EndZ=0
    g14: LineSegment StartX=-10.15 StartY=-12 StartZ=0 EndX=-7.79258 EndY=-12 EndZ=0
    g15: Circle CenterX=-6.2215 CenterY=-2 CenterZ=0 NormalX=0 NormalY=0 NormalZ=1 AngleXU=0 Radius=1
    g16: Circle CenterX=-6.22762 CenterY=-2.58724 CenterZ=0 NormalX=0 NormalY=0 NormalZ=1 AngleXU=0 Radius=1
    g17: Circle CenterX=-6.32538 CenterY=-4 CenterZ=0 NormalX=0 NormalY=0 NormalZ=1 AngleXU=0 Radius=1
    g18: BSplineCurve PolesCount=3 KnotsCount=2 Degree=2 IsPeriodic=0
    g19: GeomPoint X=-6.2215 Y=-2 Z=0
    g20: GeomPoint X=-6.32538 Y=-4 Z=0
    g21: Circle CenterX=-6.48644 CenterY=-5.99526 CenterZ=0 NormalX=0 NormalY=0 NormalZ=1 AngleXU=0 Radius=1
    g22: Circle CenterX=-6.58486 CenterY=-6.99526 CenterZ=0 NormalX=0 NormalY=0 NormalZ=1 AngleXU=0 Radius=1
    g23: Circle CenterX=-6.77343 CenterY=-8 CenterZ=0 NormalX=0 NormalY=0 NormalZ=1 AngleXU=0 Radius=1
    g24: BSplineCurve PolesCount=3 KnotsCount=2 Degree=2 IsPeriodic=0
    g25: GeomPoint X=-6.48644 Y=-5.99526 Z=0
    g26: GeomPoint X=-6.77343 Y=-8 Z=0
    g27: Circle CenterX=-7.19003 CenterY=-10 CenterZ=0 NormalX=0 NormalY=0 NormalZ=1 AngleXU=0 Radius=1
    g28: Circle CenterX=-7.44407 CenterY=-11.0915 CenterZ=0 NormalX=0 NormalY=0 NormalZ=1 AngleXU=0 Radius=1
    g29: Circle CenterX=-7.79258 CenterY=-12 CenterZ=0 NormalX=0 NormalY=0 NormalZ=1 AngleXU=0 Radius=1
    g30: BSplineCurve PolesCount=3 KnotsCount=2 Degree=2 IsPeriodic=0
    g31: GeomPoint X=-7.19003 Y=-10 Z=0
    g32: GeomPoint X=-7.79258 Y=-12 Z=0
    g33: Circle CenterX=-8.70761 CenterY=-14 CenterZ=0 NormalX=0 NormalY=0 NormalZ=1 AngleXU=0 Radius=1
    g34: Circle CenterX=-9.33087 CenterY=-15.1837 CenterZ=0 NormalX=0 NormalY=0 NormalZ=1 AngleXU=0 Radius=1
    g35: Circle CenterX=-10.1571 CenterY=-16 CenterZ=0 NormalX=0 NormalY=0 NormalZ=1 AngleXU=0 Radius=1
    g36: BSplineCurve PolesCount=3 KnotsCount=2 Degree=2 IsPeriodic=0
    g37: GeomPoint X=-8.70761 Y=-14 Z=0
    g38: GeomPoint X=-10.1571 Y=-16 Z=0
    g39: Circle CenterX=-12.8401 CenterY=-17.6958 CenterZ=0 NormalX=0 NormalY=0 NormalZ=1 AngleXU=0 Radius=1
    g40: Circle CenterX=-13.3521 CenterY=-17.9027 CenterZ=0 NormalX=0 NormalY=0 NormalZ=1 AngleXU=0 Radius=1
    g41: Circle CenterX=-14 CenterY=-18 CenterZ=0 NormalX=0 NormalY=0 NormalZ=1 AngleXU=0 Radius=1
    g42: BSplineCurve PolesCount=3 KnotsCount=2 Degree=2 IsPeriodic=0
    g43: GeomPoint X=-12.8401 Y=-17.6958 Z=0
    g44: GeomPoint X=-14 Y=-18 Z=0
    g45: LineSegment StartX=-6.2 StartY=0 StartZ=0 EndX=-7.2 EndY=0 EndZ=0
    g46: LineSegment StartX=-7.2 StartY=0 StartZ=0 EndX=-7.2 EndY=-2 EndZ=0
    g47: LineSegment StartX=-7.2 StartY=-2 StartZ=0 EndX=-6.2215 EndY=-2 EndZ=0
    g48: LineSegment StartX=-6.32538 StartY=-4 StartZ=0 EndX=-7.65538 EndY=-4 EndZ=0
    g49: LineSegment StartX=-7.65538 StartY=-4 StartZ=0 EndX=-7.65538 EndY=-5.99526 EndZ=0
    g50: LineSegment StartX=-7.65538 StartY=-5.99526 StartZ=0 EndX=-6.48644 EndY=-5.99526 EndZ=0
    g51: LineSegment StartX=-6.77343 StartY=-8 StartZ=0 EndX=-8.43343 EndY=-8 EndZ=0
    g52: LineSegment StartX=-8.43343 StartY=-8 StartZ=0 EndX=-8.43343 EndY=-10 EndZ=0
    g53: LineSegment StartX=-8.43343 StartY=-10 StartZ=0 EndX=-7.19003 EndY=-10 EndZ=0
  constraints (112):
    c: Horizontal(g0)
    c: Distance(g0) = 2
    c: Block(g0)
    c: Vertical(g1)
    c: Coincident(g2,g0)
    c: Vertical(g2)
    c: Block(g2)
    c: Coincident(g6,g2)
    c: Weight(g3) = 1
    c: Equal(g3,g4)
    c: Equal(g3,g5)
    c: InternalAlignment(g3,g6)
    c: InternalAlignment(g4,g6)
    c: InternalAlignment(g5,g6)
    c: InternalAlignment(g7,g6)
    c: InternalAlignment(g8,g6)
    c: Block(g6)
    c: Coincident(g9,g1)
    c: Coincident(g9,g6)
    c: Horizontal(g9)
    c: Vertical(g10)
    c: Block(g10)
    c: Horizontal(g11)
    c: Block(g11)
    c: Coincident(g12,g10)
    c: Horizontal(g12)
    c: Block(g12)
    c: Coincident(g13,g11)
    c: Vertical(g13)
    c: Block(g13)
    c: Coincident(g14,g10)
    c: Horizontal(g14)
    c: Block(g14)
    c: Block(g9)
    c: Block(g1)
    c: Weight(g15) = 1
    c: Equal(g15,g16)
    c: Equal(g15,g17)
    c: InternalAlignment(g15,g18)
    c: InternalAlignment(g16,g18)
    c: InternalAlignment(g17,g18)
    c: InternalAlignment(g19,g18)
    c: InternalAlignment(g20,g18)
    c: Weight(g21) = 1
    c: Equal(g21,g22)
    c: Equal(g21,g23)
    c: InternalAlignment(g21,g24)
    c: InternalAlignment(g22,g24)
    c: InternalAlignment(g23,g24)
    c: InternalAlignment(g25,g24)
    c: InternalAlignment(g26,g24)
    c: Weight(g27) = 1
    c: Equal(g27,g28)
    c: Equal(g27,g29)
    c: Coincident(g30,g14)
    c: InternalAlignment(g27,g30)
    c: InternalAlignment(g28,g30)
    c: InternalAlignment(g29,g30)
    c: InternalAlignment(g31,g30)
    c: InternalAlignment(g32,g30)
    c: Coincident(g36,g12)
    c: Weight(g33) = 1
    c: Equal(g33,g34)
    c: Equal(g33,g35)
    c: Coincident(g36,g11)
    c: InternalAlignment(g33,g36)
    c: InternalAlignment(g34,g36)
    c: InternalAlignment(g35,g36)
    c: InternalAlignment(g37,g36)
    c: InternalAlignment(g38,g36)
    c: Coincident(g42,g13)
    c: Weight(g39) = 1
    c: Equal(g39,g40)
    c: Equal(g39,g41)
    c: Coincident(g42,g1)
    c: InternalAlignment(g39,g42)
    c: InternalAlignment(g40,g42)
    c: InternalAlignment(g41,g42)
    c: InternalAlignment(g43,g42)
    c: InternalAlignment(g44,g42)
    c: Block(g18)
    c: Block(g24)
    c: Block(g30)
    c: Block(g36)
    c: Block(g42)
    c: Horizontal(g45)
    c: Coincident(g45,g0)
    c: Vertical(g46)
    c: Coincident(g46,g45)
    c: Coincident(g47,g46)
    c: Coincident(g47,g18)
    c: Horizontal(g47)
    c: Block(g46)
    c: Coincident(g48,g18)
    c: Horizontal(g48)
    c: Distance(g48) = 1.33
    c: Vertical(g49)
    c: Coincident(g49,g48)
    c: Coincident(g50,g49)
    c: Coincident(g50,g24)
    c: Horizontal(g50)
    c: Tangent(g50,g22)
    c: Horizontal(g51)
    c: Coincident(g51,g24)
    c: Block(g51)
    c: Vertical(g52)
    c: Block(g52)
    c: Coincident(g52,g51)
    c: Coincident(g53,g52)
    c: Coincident(g53,g30)
    c: Horizontal(g53)
    c: Distance(g1) = 8.5
FEATURE [Part::Feature] Face024
  shape: bbox 9.8 x 26.5 x 2e-07 mm, 1 faces, 0 solids (baked)
FEATURE [Part::Revolution] Revolve024
  Angle = 360
  Axis = (0,1,0)
  Base = (0,0,0)
  FaceMakerClass = Part::FaceMakerBullseye
  Placement = pos=(0,0,0) rot=(0,0,1;1.5708rad)
  Solid = false
  Source = -> Face024
  Symmetric = false
FEATURE [Part::Feature] Face025
  shape: bbox 9.8 x 26.5 x 2e-07 mm, 1 faces, 0 solids (baked)
FEATURE [Part::Revolution] Revolve025
  Angle = 360
  Axis = (0,1,0)
  Base = (0,0,0)
  FaceMakerClass = Part::FaceMakerBullseye
  Placement = pos=(0,0,0) rot=(0,0,1;1.5708rad)
  Solid = false
  Source = -> Face025
  Symmetric = false
FEATURE [Part::MultiFuse] Fusion033
  Placement = pos=(-18,19,36) rot=(0,0,1;0rad)
  Shapes = -> [Revolve025,Revolve024]
FEATURE [Part::Cylinder] Cylinder014
  Angle = 360
  AttacherType = Attacher::AttachEngine3D
  Height = 20
  Placement = pos=(0,0,36.15) rot=(0,0,1;0rad)
  Radius = 14.3
FEATURE [Part::Cylinder] Cylinder015
  Angle = 360
  AttacherType = Attacher::AttachEngine3D
  Height = 10
  Placement = pos=(0,0,36.15) rot=(0,0,1;0rad)
  Radius = 4
FEATURE [Part::MultiFuse] Fusion034  label="removeToCreteHoleForPlugHousing004"
  Placement = pos=(-42,19,36) rot=(0,1,0;1.5708rad)
  Shapes = -> [Cylinder014,Cylinder015]
FEATURE [Part::Cut] Cut008  label="top004"
  Base = -> Cut004
  Placement = pos=(-1,0,0) rot=(0,0,1;0rad)
  Tool = -> Fusion034
FEATURE [Part::Box] Box005  label="Cube005"
  AttacherType = Attacher::AttachEngine3D
  Height = 28
  Length = 3
  Placement = pos=(110.7,19,22) rot=(0,0,1;0rad)
  Width = 15.7
FEATURE [Part::Cylinder] Cylinder016
  Angle = 360
  AttacherType = Attacher::AttachEngine3D
  Height = 10
  Placement = pos=(0,0,36.15) rot=(0,0,1;0rad)
  Radius = 4
FEATURE [Part::Cylinder] Cylinder017
  Angle = 360
  AttacherType = Attacher::AttachEngine3D
  Height = 20
  Placement = pos=(0,0,36.15) rot=(0,0,1;0rad)
  Radius = 10.3
FEATURE [Part::MultiFuse] Fusion035  label="removeToCreteHoleForPlugHousing005"
  Placement = pos=(70,19,36) rot=(0,1,0;1.5708rad)
  Shapes = -> [Cylinder017,Cylinder016]
FEATURE [Part::Cut] Cut009  label="plugHousingTab001"
  Base = -> Box005
  Placement = pos=(-107.4,-14,0) rot=(0,0,1;0rad)
  Tool = -> Fusion035
FEATURE [Part::Box] Box006  label="Cube006"
  AttacherType = Attacher::AttachEngine3D
  Height = 28
  Length = 3
  Placement = pos=(110.7,19,22) rot=(0,0,1;0rad)
  Width = 15.7
FEATURE [Part::Cylinder] Cylinder018
  Angle = 360
  AttacherType = Attacher::AttachEngine3D
  Height = 10
  Placement = pos=(0,0,36.15) rot=(0,0,1;0rad)
  Radius = 4
FEATURE [Part::Cylinder] Cylinder019
  Angle = 360
  AttacherType = Attacher::AttachEngine3D
  Height = 20
  Placement = pos=(0,0,36.15) rot=(0,0,1;0rad)
  Radius = 10.3
FEATURE [Part::MultiFuse] Fusion036  label="removeToCreteHoleForPlugHousing006"
  Placement = pos=(70,19,36) rot=(0,1,0;1.5708rad)
  Shapes = -> [Cylinder019,Cylinder018]
FEATURE [Part::Cut] Cut010  label="plugHousingTab002"
  Base = -> Box006
  Placement = pos=(-107.4,-14,0) rot=(0,0,1;0rad)
  Tool = -> Fusion036
FEATURE [Part::MultiFuse] Fusion037
  Placement = pos=(9.6,23,0) rot=(0,0,1;3.14159rad)
  Shapes = -> [Cut009,Cut010]
FEATURE [Part::Box] Box  label="Cube"
  AttacherType = Attacher::AttachEngine3D
  Height = 10
  Length = 3
  Placement = pos=(3.3,4,12) rot=(0,0,1;0rad)
  Width = 10
FEATURE [Part::Fillet] Fillet004
  Base = -> Fusion028
  Edges = 1 edges r=2: [Edge25]
FEATURE [Part::Fillet] Fillet005  label="plugHousing046"
  Base = -> Fillet004
  Edges = 1 edges r=2: [Edge8]
FEATURE [Part::Fillet] Fillet006
  Base = -> Box
  Edges = 1 edges r=2: [Edge11]
FEATURE [Part::Box] Box007  label="Cube007"
  AttacherType = Attacher::AttachEngine3D
  Height = 10
  Length = 3
  Placement = pos=(3.3,4,50) rot=(0,0,1;0rad)
  Width = 10
FEATURE [Part::Fillet] Fillet007
  Base = -> Box007
  Edges = 1 edges r=2: [Edge12]
FEATURE [Part::Box] Box008  label="Cube008"
  AttacherType = Attacher::AttachEngine3D
  Height = 28
  Length = 4
  Placement = pos=(5,0,22) rot=(0,0,1;0rad)
  Width = 10
FEATURE [Part::Fillet] Fillet008
  Base = -> Box008
  Edges = 1 edges r=1: [Edge7]
FEATURE [Part::Fillet] Fillet009
  Base = -> Fillet008
  Edges = 1 edges r=2: [Edge5]
FEATURE [Part::Fillet] Fillet010
  Base = -> Fillet009
  Edges = 1 edges r=2: [Edge2]
FEATURE [Sketcher::SketchObject] Sketch009  label="topSketch003"
  FullyConstrained = true
  sketch-geometry (4):
    g0: LineSegment StartX=16.8446 StartY=31.512 StartZ=0 EndX=16.3251 EndY=34.4666 EndZ=0
    g1: ArcOfCircle CenterX=19 CenterY=19.2524 CenterZ=0 NormalX=0 NormalY=0 NormalZ=1 AngleXU=0 Radius=15.4476 StartAngle=1.74483 EndAngle=2.72717
    g2: ArcOfCircle CenterX=19 CenterY=19.2524 CenterZ=0 NormalX=0 NormalY=0 NormalZ=1 AngleXU=0 Radius=12.4476 StartAngle=1.74483 EndAngle=2.73189
    g3: LineSegment StartX=4.86004 StartY=25.4725 StartZ=0 EndX=7.58253 EndY=24.2107 EndZ=0
  constraints (7):
    c: Block(g0)
    c: Coincident(g1,g0)
    c: Coincident(g2,g0)
    c: Coincident(g3,g1)
    c: Coincident(g3,g2)
    c: Block(g1)
    c: Block(g2)
FEATURE [Part::Extrusion] Extrude008
  Base = -> Sketch009
  Dir = (0,0,1)
  DirMode = 2
  FaceMakerClass = Part::FaceMakerBullseye
  LengthFwd = 10
  LengthRev = 0
  Placement = pos=(0,0,31) rot=(0,0,1;0rad)
  Solid = true
  Symmetric = false
FEATURE [Part::Cylinder] Cylinder020
  Angle = 360
  AttacherType = Attacher::AttachEngine3D
  Height = 20
  Placement = pos=(0,0,36.15) rot=(0,0,1;0rad)
  Radius = 8.2
FEATURE [Part::Cylinder] Cylinder021
  Angle = 360
  AttacherType = Attacher::AttachEngine3D
  Height = 10
  Placement = pos=(0,0,36.15) rot=(0,0,1;0rad)
  Radius = 4
FEATURE [Part::MultiFuse] Fusion038  label="removeToCreteHoleForPlugHousing007"
  Placement = pos=(-42,19,36) rot=(0,1,0;1.5708rad)
  Shapes = -> [Cylinder020,Cylinder021]
FEATURE [Part::Cut] Cut011
  Base = -> Extrude008
  Tool = -> Fusion038
FEATURE [Part::Fillet] Fillet011
  Base = -> Cut011
  Edges = 1 edges r=2: [Edge1]
FEATURE [Part::Fillet] Fillet012
  Base = -> Fillet011
  Edges = 1 edges r=2.5: [Edge1]
FEATURE [Part::Fillet] Fillet013
  Base = -> Fillet012
  Edges = 1 edges r=2.5: [Edge2]
FEATURE [Part::Box] Box010  label="Cube010"
  AttacherType = Attacher::AttachEngine3D
  Height = 16
  Length = 8
  Placement = pos=(12.7,31.52,28) rot=(0,0,1;0rad)
  Width = 4
FEATURE [Sketcher::SketchObject] Sketch010  label="topSketch004"
  FullyConstrained = true
  sketch-geometry (4):
    g0: LineSegment StartX=16.8446 StartY=31.512 StartZ=0 EndX=16.3251 EndY=34.4666 EndZ=0
    g1: ArcOfCircle CenterX=19 CenterY=19.2524 CenterZ=0 NormalX=0 NormalY=0 NormalZ=1 AngleXU=0 Radius=15.4476 StartAngle=1.74483 EndAngle=2.72717
    g2: ArcOfCircle CenterX=19 CenterY=19.2524 CenterZ=0 NormalX=0 NormalY=0 NormalZ=1 AngleXU=0 Radius=12.4476 StartAngle=1.74483 EndAngle=2.73189
    g3: LineSegment StartX=4.86004 StartY=25.4725 StartZ=0 EndX=7.58253 EndY=24.2107 EndZ=0
  constraints (7):
    c: Block(g0)
    c: Coincident(g1,g0)
    c: Coincident(g2,g0)
    c: Coincident(g3,g1)
    c: Coincident(g3,g2)
    c: Block(g1)
    c: Block(g2)
FEATURE [Part::Cylinder] Cylinder022
  Angle = 360
  AttacherType = Attacher::AttachEngine3D
  Height = 10
  Placement = pos=(0,0,36.15) rot=(0,0,1;0rad)
  Radius = 4
FEATURE [Sketcher::SketchObject] Sketch011  label="topSketch005"
  FullyConstrained = true
  sketch-geometry (4):
    g0: LineSegment StartX=16.8446 StartY=31.512 StartZ=0 EndX=16.3251 EndY=34.4666 EndZ=0
    g1: ArcOfCircle CenterX=19 CenterY=19.2524 CenterZ=0 NormalX=0 NormalY=0 NormalZ=1 AngleXU=0 Radius=15.4476 StartAngle=1.74483 EndAngle=2.72717
    g2: ArcOfCircle CenterX=19 CenterY=19.2524 CenterZ=0 NormalX=0 NormalY=0 NormalZ=1 AngleXU=0 Radius=12.4476 StartAngle=1.74483 EndAngle=2.73189
    g3: LineSegment StartX=4.86004 StartY=25.4725 StartZ=0 EndX=7.58253 EndY=24.2107 EndZ=0
  constraints (7):
    c: Block(g0)
    c: Coincident(g1,g0)
    c: Coincident(g2,g0)
    c: Coincident(g3,g1)
    c: Coincident(g3,g2)
    c: Block(g1)
    c: Block(g2)
FEATURE [Part::Extrusion] Extrude010
  Base = -> Sketch011
  Dir = (0,0,1)
  DirMode = 2
  FaceMakerClass = Part::FaceMakerBullseye
  LengthFwd = 10.6
  LengthRev = 0
  Placement = pos=(0,0,31) rot=(0,0,1;0rad)
  Solid = true
  Symmetric = false
FEATURE [Part::Cylinder] Cylinder023
  Angle = 360
  AttacherType = Attacher::AttachEngine3D
  Height = 20
  Placement = pos=(0,0,36.15) rot=(0,0,1;0rad)
  Radius = 8.2
FEATURE [Part::MultiFuse] Fusion039  label="removeToCreteHoleForPlugHousing008"
  Placement = pos=(-42,19,36) rot=(0,1,0;1.5708rad)
  Shapes = -> [Cylinder023,Cylinder022]
FEATURE [Part::Cut] Cut012
  Base = -> Extrude010
  Placement = pos=(0,0,-0.3) rot=(0,0,1;0rad)
  Tool = -> Fusion039
FEATURE [Part::Cut] Cut013
  Base = -> Box010
  Tool = -> Cut012
FEATURE [Part::Fillet] Fillet014
  Base = -> Cut013
  Edges = 1 edges r=0.7: [Edge13]
FEATURE [Part::Fillet] Fillet015
  Base = -> Fillet014
  Edges = 1 edges r=0.7: [Edge13]
FEATURE [Part::Fillet] Fillet016
  Base = -> Fillet015
  Edges = 1 edges r=0.7: [Edge16]
FEATURE [Part::Fillet] Fillet017
  Base = -> Fillet016
  Edges = 1 edges r=0.7: [Edge11]
FEATURE [Part::Fillet] Fillet018
  Base = -> Fillet017
  Edges = 1 edges r=0.7: [Edge10]
FEATURE [Part::Fillet] Fillet019
  Base = -> Fillet018
  Edges = 1 edges r=1.2: [Edge5]
FEATURE [Part::Fillet] Fillet020
  Base = -> Fillet019
  Edges = 1 edges r=1.2: [Edge12]
FEATURE [Part::Fillet] Fillet021
  Base = -> Fillet020
  Edges = 1 edges r=2: [Edge1]
  Placement = pos=(0.3,0,0) rot=(0,0,1;0rad)
FEATURE [Part::MultiFuse] Fusion040  label="top005"
  Shapes = -> [Cut008,Fillet021]
FEATURE [Part::MultiFuse] Fusion041  label="wireHolder"
  Shapes = -> [Fusion033,Fillet013]
FEATURE [Part::MultiFuse] Fusion042
  Shapes = -> [Fillet007,Fusion041]
FEATURE [Part::MultiFuse] Fusion043  label="wireHolder001"
  Shapes = -> [Fusion042,Fillet010]
FEATURE [Part::MultiFuse] Fusion044  label="wireHolder002"
  Shapes = -> [Fillet006,Fusion037,Fusion043]
FEATURE [Part::Feature] Face026
  shape: bbox 11 x 6 x 2e-07 mm, 1 faces, 0 solids (baked)
FEATURE [Part::Revolution] Revolve026
  Angle = 360
  Axis = (0,1,0)
  Base = (0,0,0)
  FaceMakerClass = Part::FaceMakerBullseye
  Placement = pos=(30.3,-1,19.7) rot=(0,0,1;0rad)
  Solid = false
  Source = -> Face026
  Symmetric = false
FEATURE [Sketcher::SketchObject] Sketch013  label="topSketch006"
  FullyConstrained = true
  sketch-geometry (13):
    g0: LineSegment StartX=117 StartY=19 StartZ=0 EndX=117 EndY=38 EndZ=0
    g1: ArcOfCircle CenterX=98 CenterY=19 CenterZ=0 NormalX=0 NormalY=0 NormalZ=1 AngleXU=0 Radius=19 StartAngle=5.7297 EndAngle=6.28319
    g2: LineSegment StartX=0 StartY=3 StartZ=0 EndX=0 EndY=19 EndZ=0
    g3: LineSegment StartX=19 StartY=38 StartZ=0 EndX=117 EndY=38 EndZ=0
    g4: ArcOfCircle CenterX=19 CenterY=19 CenterZ=0 NormalX=0 NormalY=0 NormalZ=1 AngleXU=0 Radius=19 StartAngle=1.5708 EndAngle=3.14159
    g5: ArcOfCircle CenterX=19 CenterY=19 CenterZ=0 NormalX=0 NormalY=0 NormalZ=1 AngleXU=0 Radius=16 StartAngle=1.5708 EndAngle=3.14159
    g6: ArcOfCircle CenterX=98 CenterY=19 CenterZ=0 NormalX=0 NormalY=0 NormalZ=1 AngleXU=0 Radius=16 StartAngle=5.60905 EndAngle=6.28319
    g7: LineSegment StartX=114 StartY=19 StartZ=0 EndX=114 EndY=35 EndZ=0
    g8: LineSegment StartX=110.5 StartY=9.01251 StartZ=0 EndX=114.163 EndY=9.01251 EndZ=0
    g9: LineSegment StartX=114 StartY=35 StartZ=0 EndX=19 EndY=35 EndZ=0
    g10: LineSegment StartX=0 StartY=3 StartZ=0 EndX=0 EndY=0 EndZ=0
    g11: LineSegment StartX=3 StartY=0 StartZ=0 EndX=0 EndY=0 EndZ=0
    g12: LineSegment StartX=3 StartY=19 StartZ=0 EndX=3 EndY=0 EndZ=0
  constraints (33):
    c: Vertical(g0)
    c: Distance(g0) = 19
    c: Block(g0)
    c: Coincident(g1,g0)
    c: Block(g1)
    c: Vertical(g2)
    c: Block(g2)
    c: Coincident(g3,g0)
    c: Horizontal(g3)
    c: Distance(g3) = 98
    c: Coincident(g4,g3)
    c: Coincident(g4,g2)
    c: Block(g4)
    c: Coincident(g5,g4)
    c: Coincident(g6,g1)
    c: Block(g6)
    c: Block(g5)
    c: Coincident(g7,g6)
    c: Vertical(g7)
    c: Coincident(g8,g6)
    c: Coincident(g8,g1)
    c: Coincident(g9,g7)
    c: Coincident(g9,g5)
    c: Horizontal(g9)
    c: Tangent(g9,g5)
    c: Coincident(g10,g2)
    c: Distance(g10) = 3
    c: Vertical(g10)
    c: Coincident(g11,g10)
    c: Horizontal(g11)
    c: Coincident(g12,g5)
    c: Coincident(g12,g11)
    c: Vertical(g12)
FEATURE [Part::Extrusion] Extrude011  label="top006"
  Base = -> Sketch013
  Dir = (0,0,1)
  DirMode = 2
  FaceMakerClass = Part::FaceMakerBullseye
  LengthFwd = 72
  LengthRev = 0
  Solid = true
  Symmetric = false
FEATURE [Sketcher::SketchObject] Sketch014
  FullyConstrained = true
  MapMode = 3
  Placement = pos=(0,0,0) rot=(1,0,0;1.5708rad)
  Support = -> [Extrude011]
  sketch-geometry (8):
    g0: Circle CenterX=80.351 CenterY=-67.6202 CenterZ=0 NormalX=0 NormalY=0 NormalZ=1 AngleXU=0 Radius=2
    g1: Circle CenterX=80.351 CenterY=-67.6202 CenterZ=0 NormalX=0 NormalY=0 NormalZ=1 AngleXU=0 Radius=3
    g2: Circle CenterX=80.351 CenterY=-4.92017 CenterZ=0 NormalX=0 NormalY=0 NormalZ=1 AngleXU=0 Radius=2
    g3: Circle CenterX=80.351 CenterY=-4.92017 CenterZ=0 NormalX=0 NormalY=0 NormalZ=1 AngleXU=0 Radius=3
    g4: Circle CenterX=23.851 CenterY=-4.92017 CenterZ=0 NormalX=0 NormalY=0 NormalZ=1 AngleXU=0 Radius=2
    g5: Circle CenterX=23.851 CenterY=-4.92017 CenterZ=0 NormalX=0 NormalY=0 NormalZ=1 AngleXU=0 Radius=3
    g6: Circle CenterX=23.851 CenterY=-67.6202 CenterZ=0 NormalX=0 NormalY=0 NormalZ=1 AngleXU=0 Radius=2
    g7: Circle CenterX=23.851 CenterY=-67.6202 CenterZ=0 NormalX=0 NormalY=0 NormalZ=1 AngleXU=0 Radius=3
  constraints (8):
    c: Block(g3)
    c: Block(g2)
    c: Block(g1)
    c: Block(g0)
    c: Block(g6)
    c: Block(g7)
    c: Block(g4)
    c: Block(g5)
FEATURE [Part::Feature] Face027
  shape: bbox 11 x 6 x 2e-07 mm, 1 faces, 0 solids (baked)
FEATURE [Part::Revolution] Revolve027
  Angle = 360
  Axis = (0,1,0)
  Base = (0,0,0)
  FaceMakerClass = Part::FaceMakerBullseye
  Placement = pos=(30.3,-1,51.7) rot=(0,0,1;0rad)
  Solid = false
  Source = -> Face027
  Symmetric = false
FEATURE [Part::Feature] Face028
  shape: bbox 11 x 6 x 2e-07 mm, 1 faces, 0 solids (baked)
FEATURE [Part::Revolution] Revolve028
  Angle = 360
  Axis = (0,1,0)
  Base = (0,0,0)
  FaceMakerClass = Part::FaceMakerBullseye
  Placement = pos=(62.3,-1,19.7) rot=(0,0,1;0rad)
  Solid = false
  Source = -> Face028
  Symmetric = false
FEATURE [Part::Feature] Face029
  shape: bbox 11 x 6 x 2e-07 mm, 1 faces, 0 solids (baked)
FEATURE [Part::Revolution] Revolve029
  Angle = 360
  Axis = (0,1,0)
  Base = (0,0,0)
  FaceMakerClass = Part::FaceMakerBullseye
  Placement = pos=(62.3,-1,51.7) rot=(0,0,1;0rad)
  Solid = false
  Source = -> Face029
  Symmetric = false
FEATURE [Part::Feature] Wire
  shape: bbox 11 x 5.2 x 2e-07 mm, 0 faces, 0 solids (baked)
FEATURE [Part::Revolution] Revolve030
  Angle = 360
  Axis = (0,1,0)
  Base = (0,0,0)
  FaceMakerClass = Part::FaceMakerBullseye
  Placement = pos=(30.3,38,19.7) rot=(0,0,1;0rad)
  Solid = true
  Source = -> Wire
  Symmetric = false
FEATURE [Part::Feature] Wire001
  shape: bbox 11 x 5.2 x 2e-07 mm, 0 faces, 0 solids (baked)
FEATURE [Part::Revolution] Revolve031
  Angle = 360
  Axis = (0,1,0)
  Base = (0,0,0)
  FaceMakerClass = Part::FaceMakerBullseye
  Placement = pos=(30.3,38,51.7) rot=(0,0,1;0rad)
  Solid = true
  Source = -> Wire001
  Symmetric = false
FEATURE [Part::Feature] Wire002
  shape: bbox 11 x 5.2 x 2e-07 mm, 0 faces, 0 solids (baked)
FEATURE [Part::Revolution] Revolve032
  Angle = 360
  Axis = (0,1,0)
  Base = (0,0,0)
  FaceMakerClass = Part::FaceMakerBullseye
  Placement = pos=(62.3,38,51.7) rot=(0,0,1;0rad)
  Solid = true
  Source = -> Wire002
  Symmetric = false
FEATURE [Part::Feature] Wire003
  shape: bbox 11 x 5.2 x 2e-07 mm, 0 faces, 0 solids (baked)
FEATURE [Part::Revolution] Revolve033
  Angle = 360
  Axis = (0,1,0)
  Base = (0,0,0)
  FaceMakerClass = Part::FaceMakerBullseye
  Placement = pos=(62.3,38,19.7) rot=(0,0,1;0rad)
  Solid = true
  Source = -> Wire003
  Symmetric = false
FEATURE [Part::MultiFuse] Fusion045  label="altRandScrewHousing"
  Shapes = -> [Revolve029,Revolve027,Revolve028,Revolve026]
FEATURE [Part::MultiFuse] Fusion046  label="fanScrewHousing"
  Shapes = -> [Revolve033,Revolve032,Revolve031,Revolve030]
FEATURE [Sketcher::SketchObject] Sketch015
  FullyConstrained = true
  sketch-geometry (17):
    g0: Circle CenterX=-3.5 CenterY=23.5 CenterZ=0 NormalX=0 NormalY=0 NormalZ=1 AngleXU=0 Radius=1
    g1: Circle CenterX=-1 CenterY=15.25 CenterZ=0 NormalX=0 NormalY=0 NormalZ=1 AngleXU=0 Radius=1
    g2: Circle CenterX=-3.5 CenterY=7 CenterZ=0 NormalX=0 NormalY=0 NormalZ=1 AngleXU=0 Radius=1
    g3: BSplineCurve PolesCount=3 KnotsCount=2 Degree=2 IsPeriodic=0
    g4: GeomPoint X=-3.5 Y=23.5 Z=0
    g5: GeomPoint X=-3.5 Y=7 Z=0
    g6: Circle CenterX=-4.8 CenterY=30.5 CenterZ=0 NormalX=0 NormalY=0 NormalZ=1 AngleXU=0 Radius=1
    g7: Circle CenterX=-3.5 CenterY=30.5 CenterZ=0 NormalX=0 NormalY=0 NormalZ=1 AngleXU=0 Radius=1
    g8: Circle CenterX=-3.5 CenterY=29.2 CenterZ=0 NormalX=0 NormalY=0 NormalZ=1 AngleXU=0 Radius=1
    g9: BSplineCurve PolesCount=3 KnotsCount=2 Degree=2 IsPeriodic=0
    g10: GeomPoint X=-4.8 Y=30.5 Z=0
    g11: GeomPoint X=-3.5 Y=29.2 Z=0
    g12: LineSegment StartX=-3.5 StartY=29.2 StartZ=0 EndX=-3.5 EndY=23.5 EndZ=0
    g13: LineSegment StartX=-4.8 StartY=30.5 StartZ=0 EndX=0 EndY=30.5 EndZ=0
    g14: LineSegment StartX=-3.5 StartY=0.3 StartZ=0 EndX=0 EndY=0.3 EndZ=0
    g15: LineSegment StartX=-3.5 StartY=0.3 StartZ=0 EndX=-3.5 EndY=7 EndZ=0
    g16: LineSegment StartX=0 StartY=0.3 StartZ=0 EndX=0 EndY=30.5 EndZ=0
  constraints (33):
    c: Weight(g0) = 1
    c: Equal(g0,g1)
    c: Equal(g0,g2)
    c: InternalAlignment(g0,g3)
    c: InternalAlignment(g1,g3)
    c: InternalAlignment(g2,g3)
    c: InternalAlignment(g4,g3)
    c: InternalAlignment(g5,g3)
    c: Block(g3)
    c: Weight(g6) = 1
    c: Equal(g6,g7)
    c: Equal(g6,g8)
    c: InternalAlignment(g6,g9)
    c: InternalAlignment(g7,g9)
    c: InternalAlignment(g8,g9)
    c: InternalAlignment(g10,g9)
    c: InternalAlignment(g11,g9)
    c: Block(g9)
    c: Coincident(g12,g9)
    c: Coincident(g12,g3)
    c: Vertical(g12)
    c: Coincident(g13,g9)
    c: Horizontal(g13)
    c: Distance(g13) = 4.8
    c: Horizontal(g14)
    c: Block(g14)
    c: Coincident(g15,g14)
    c: Coincident(g15,g3)
    c: Vertical(g15)
    c: Coincident(g16,g14)
    c: Coincident(g16,g13)
    c: Vertical(g16)
    c: Tangent(g16,g1)
FEATURE [Sketcher::SketchObject] Sketch016
  FullyConstrained = true
  sketch-geometry (16):
    g0: Circle CenterX=-3.5 CenterY=23.5 CenterZ=0 NormalX=0 NormalY=0 NormalZ=1 AngleXU=0 Radius=1
    g1: Circle CenterX=-1 CenterY=15.25 CenterZ=0 NormalX=0 NormalY=0 NormalZ=1 AngleXU=0 Radius=1
    g2: Circle CenterX=-3.5 CenterY=7 CenterZ=0 NormalX=0 NormalY=0 NormalZ=1 AngleXU=0 Radius=1
    g3: BSplineCurve PolesCount=3 KnotsCount=2 Degree=2 IsPeriodic=0
    g4: GeomPoint X=-3.5 Y=23.5 Z=0
    g5: GeomPoint X=-3.5 Y=7 Z=0
    g6: LineSegment StartX=-3.5 StartY=28.2 StartZ=0 EndX=-3.5 EndY=23.5 EndZ=0
    g7: LineSegment StartX=0 StartY=29.5 StartZ=0 EndX=0 EndY=30 EndZ=0
    g8: LineSegment StartX=-3.5 StartY=28.2 StartZ=0 EndX=-3.5 EndY=30 EndZ=0
    g9: LineSegment StartX=0 StartY=30 StartZ=0 EndX=0 EndY=30.5 EndZ=0
    g10: LineSegment StartX=0 StartY=30.5 StartZ=0 EndX=-3.5 EndY=30.5 EndZ=0
    g11: LineSegment StartX=-3.5 StartY=30.5 StartZ=0 EndX=-3.5 EndY=30 EndZ=0
    g12: LineSegment StartX=0 StartY=29.5 StartZ=0 EndX=0 EndY=5 EndZ=0
    g13: LineSegment StartX=-3.5 StartY=0.3 StartZ=0 EndX=-3.5 EndY=7 EndZ=0
    g14: LineSegment StartX=-3.5 StartY=0.3 StartZ=0 EndX=0 EndY=0.3 EndZ=0
    g15: LineSegment StartX=0 StartY=5 StartZ=0 EndX=0 EndY=0.3 EndZ=0
  constraints (39):
    c: Weight(g0) = 1
    c: Equal(g0,g1)
    c: Equal(g0,g2)
    c: InternalAlignment(g0,g3)
    c: InternalAlignment(g1,g3)
    c: InternalAlignment(g2,g3)
    c: InternalAlignment(g4,g3)
    c: InternalAlignment(g5,g3)
    c: Block(g3)
    c: Coincident(g6,g3)
    c: Vertical(g6)
    c: Vertical(g7)
    c: Distance(g7) = 0.5
    c: Coincident(g8,g6)
    c: Vertical(g8)
    c: Block(g6)
    c: Block(g7)
    c: Vertical(g9)
    c: Equal(g7,g9) = 0.5
    c: Block(g9)
    c: Coincident(g9,g7)
    c: Horizontal(g10)
    c: Coincident(g10,g9)
    c: Coincident(g11,g10)
    c: Coincident(g11,g8)
    c: Vertical(g11)
    c: Block(g11)
    c: Coincident(g12,g7)
    c: Vertical(g12)
    c: Coincident(g13,g3)
    c: Vertical(g13)
    c: Distance(g13) = 6.7
    c: Coincident(g14,g13)
    c: Horizontal(g14)
    c: Block(g14)
    c: Coincident(g15,g12)
    c: Coincident(g15,g14)
    c: Vertical(g15)
    c: Block(g15)
FEATURE [Sketcher::SketchObject] Sketch017
  FullyConstrained = true
  sketch-geometry (11):
    g0: LineSegment StartX=-3.5 StartY=1e-16 StartZ=0 EndX=-1.6 EndY=1e-16 EndZ=0
    g1: LineSegment StartX=-1.6 StartY=1e-16 StartZ=0 EndX=-1.6 EndY=1.5 EndZ=0
    g2: LineSegment StartX=-3.5 StartY=1.5 StartZ=0 EndX=-1.6 EndY=1.5 EndZ=0
    g3: LineSegment StartX=-3.5 StartY=1e-16 StartZ=0 EndX=-4.8 EndY=1e-16 EndZ=0
    g4: Circle CenterX=-3.5 CenterY=1.3 CenterZ=0 NormalX=0 NormalY=0 NormalZ=1 AngleXU=0 Radius=1
    g5: Circle CenterX=-3.5 CenterY=1e-16 CenterZ=0 NormalX=0 NormalY=0 NormalZ=1 AngleXU=0 Radius=1
    g6: Circle CenterX=-4.8 CenterY=1e-16 CenterZ=0 NormalX=0 NormalY=0 NormalZ=1 AngleXU=0 Radius=1
    g7: BSplineCurve PolesCount=3 KnotsCount=2 Degree=2 IsPeriodic=0
    g8: GeomPoint X=-3.5 Y=1.3 Z=0
    g9: GeomPoint X=-4.8 Y=1e-16 Z=0
    g10: LineSegment StartX=-3.5 StartY=1.3 StartZ=0 EndX=-3.5 EndY=1.5 EndZ=0
  constraints (24):
    c: Horizontal(g0)
    c: Distance(g0) = 1.9
    c: Block(g0)
    c: Coincident(g1,g0)
    c: Vertical(g1)
    c: Coincident(g2,g1)
    c: Horizontal(g2)
    c: Coincident(g3,g0)
    c: Horizontal(g3)
    c: Distance(g3) = 1.3
    c: Weight(g4) = 1
    c: Equal(g4,g5)
    c: Coincident(g5,g0)
    c: Equal(g4,g6)
    c: Coincident(g7,g3)
    c: InternalAlignment(g4,g7)
    c: InternalAlignment(g5,g7)
    c: InternalAlignment(g6,g7)
    c: InternalAlignment(g8,g7)
    c: InternalAlignment(g9,g7)
    c: Coincident(g10,g7)
    c: Coincident(g10,g2)
    c: Vertical(g10)
    c: Block(g10)
FEATURE [Part::Feature] Face035
  shape: bbox 3.2 x 1.5 x 2e-07 mm, 1 faces, 0 solids (baked)
FEATURE [Part::Revolution] Revolve039  label="backCaseScrewRetainer"
  Angle = 360
  Axis = (0,1,0)
  Base = (0,0,0)
  FaceMakerClass = Part::FaceMakerBullseye
  Placement = pos=(12.5,3,62) rot=(0,0,1;0rad)
  Solid = false
  Source = -> Face035
  Symmetric = false
FEATURE [Part::Feature] Face036
  shape: bbox 3.2 x 1.5 x 2e-07 mm, 1 faces, 0 solids (baked)
FEATURE [Part::Feature] Face039
  shape: bbox 4.8 x 30.2 x 2e-07 mm, 1 faces, 0 solids (baked)
FEATURE [Part::Revolution] Revolve043  label="frontCaseScrewPost002"
  Angle = 360
  Axis = (0,1,0)
  Base = (0,0,0)
  FaceMakerClass = Part::FaceMakerBullseye
  Placement = pos=(89.5,4.5,3.5) rot=(0,0,1;0rad)
  Solid = false
  Source = -> Face039
  Symmetric = false
FEATURE [Part::Feature] Face042
  shape: bbox 4.8 x 30.2 x 2e-07 mm, 1 faces, 0 solids (baked)
FEATURE [Part::Revolution] Revolve046  label="frontCaseScrewPost003"
  Angle = 360
  Axis = (0,1,0)
  Base = (0,0,0)
  FaceMakerClass = Part::FaceMakerBullseye
  Placement = pos=(89.5,4.5,68.5) rot=(0,0,1;0rad)
  Solid = false
  Source = -> Face042
  Symmetric = false
FEATURE [Part::Feature] Face043
  shape: bbox 3.2 x 1.5 x 2e-07 mm, 1 faces, 0 solids (baked)
FEATURE [Part::Revolution] Revolve047  label="frontCaseScrewRetainer002"
  Angle = 360
  Axis = (0,1,0)
  Base = (0,0,0)
  FaceMakerClass = Part::FaceMakerBullseye
  Placement = pos=(89.5,3,68.5) rot=(0,0,1;0rad)
  Solid = false
  Source = -> Face043
  Symmetric = false
FEATURE [Part::Feature] Face044
  shape: bbox 3.2 x 1.5 x 2e-07 mm, 1 faces, 0 solids (baked)
FEATURE [Part::Revolution] Revolve048  label="frontCaseScrewRetainer003"
  Angle = 360
  Axis = (0,1,0)
  Base = (0,0,0)
  FaceMakerClass = Part::FaceMakerBullseye
  Placement = pos=(89.5,3,3.5) rot=(0,0,1;0rad)
  Solid = false
  Source = -> Face044
  Symmetric = false
FEATURE [App::MeasureDistance] Distance002  label="Distance: 1.67 mm"
  Distance = 1.66921
  P1 = (99.2361,4.7524,71.7)
  P2 = (99.2347,6.42161,71.7)
FEATURE [Sketcher::SketchObject] Sketch018
  FullyConstrained = true
  sketch-geometry (7):
    g0: LineSegment StartX=0 StartY=0 StartZ=0 EndX=0 EndY=6 EndZ=0
    g1: Circle CenterX=0 CenterY=0 CenterZ=0 NormalX=0 NormalY=0 NormalZ=1 AngleXU=0 Radius=1
    g2: Circle CenterX=8 CenterY=6 CenterZ=0 NormalX=0 NormalY=0 NormalZ=1 AngleXU=0 Radius=1
    g3: BSplineCurve PolesCount=3 KnotsCount=2 Degree=2 IsPeriodic=0
    g4: GeomPoint X=0 Y=0 Z=0
    g5: GeomPoint X=8 Y=6 Z=0
    g6: LineSegment StartX=0 StartY=6 StartZ=0 EndX=8 EndY=6 EndZ=0
  constraints (14):
    c: Coincident(g0,g-1)
    c: Distance(g0) = 6
    c: Vertical(g0)
    c: Coincident(g3,g0)
    c: Weight(g1) = 1
    c: Equal(g1,g2)
    c: InternalAlignment(g1,g3)
    c: InternalAlignment(g2,g3)
    c: InternalAlignment(g4,g3)
    c: InternalAlignment(g5,g3)
    c: Block(g3)
    c: Coincident(g6,g0)
    c: Coincident(g6,g3)
    c: Horizontal(g6)
FEATURE [Part::Extrusion] Extrude012  label="caseScrewPillarBracket"
  Base = -> Sketch018
  Dir = (0,0,1)
  DirMode = 2
  FaceMakerClass = Part::FaceMakerBullseye
  LengthFwd = 2.4
  LengthRev = 0
  Placement = pos=(15.76,29,8.8) rot=(0,1,0;0rad)
  Solid = true
  Symmetric = false
FEATURE [Sketcher::SketchObject] Sketch019
  FullyConstrained = true
  sketch-geometry (7):
    g0: LineSegment StartX=0 StartY=0 StartZ=0 EndX=0 EndY=6 EndZ=0
    g1: Circle CenterX=0 CenterY=0 CenterZ=0 NormalX=0 NormalY=0 NormalZ=1 AngleXU=0 Radius=1
    g2: Circle CenterX=8 CenterY=6 CenterZ=0 NormalX=0 NormalY=0 NormalZ=1 AngleXU=0 Radius=1
    g3: BSplineCurve PolesCount=3 KnotsCount=2 Degree=2 IsPeriodic=0
    g4: GeomPoint X=0 Y=0 Z=0
    g5: GeomPoint X=8 Y=6 Z=0
    g6: LineSegment StartX=0 StartY=6 StartZ=0 EndX=8 EndY=6 EndZ=0
  constraints (14):
    c: Coincident(g0,g-1)
    c: Distance(g0) = 6
    c: Vertical(g0)
    c: Coincident(g3,g0)
    c: Weight(g1) = 1
    c: Equal(g1,g2)
    c: InternalAlignment(g1,g3)
    c: InternalAlignment(g2,g3)
    c: InternalAlignment(g4,g3)
    c: InternalAlignment(g5,g3)
    c: Block(g3)
    c: Coincident(g6,g0)
    c: Coincident(g6,g3)
    c: Horizontal(g6)
FEATURE [Part::Extrusion] Extrude013  label="caseScrewPillarBracket001"
  Base = -> Sketch019
  Dir = (0,0,1)
  DirMode = 2
  FaceMakerClass = Part::FaceMakerBullseye
  LengthFwd = 2.4
  LengthRev = 0
  Placement = pos=(15.76,29,60.8) rot=(0,0,1;0rad)
  Solid = true
  Symmetric = false
FEATURE [Sketcher::SketchObject] Sketch020
  FullyConstrained = true
  sketch-geometry (7):
    g0: LineSegment StartX=0 StartY=0 StartZ=0 EndX=0 EndY=6 EndZ=0
    g1: Circle CenterX=0 CenterY=0 CenterZ=0 NormalX=0 NormalY=0 NormalZ=1 AngleXU=0 Radius=1
    g2: Circle CenterX=8 CenterY=6 CenterZ=0 NormalX=0 NormalY=0 NormalZ=1 AngleXU=0 Radius=1
    g3: BSplineCurve PolesCount=3 KnotsCount=2 Degree=2 IsPeriodic=0
    g4: GeomPoint X=0 Y=0 Z=0
    g5: GeomPoint X=8 Y=6 Z=0
    g6: LineSegment StartX=0 StartY=6 StartZ=0 EndX=8 EndY=6 EndZ=0
  constraints (14):
    c: Coincident(g0,g-1)
    c: Distance(g0) = 6
    c: Vertical(g0)
    c: Coincident(g3,g0)
    c: Weight(g1) = 1
    c: Equal(g1,g2)
    c: InternalAlignment(g1,g3)
    c: InternalAlignment(g2,g3)
    c: InternalAlignment(g4,g3)
    c: InternalAlignment(g5,g3)
    c: Block(g3)
    c: Coincident(g6,g0)
    c: Coincident(g6,g3)
    c: Horizontal(g6)
FEATURE [Part::Extrusion] Extrude014  label="caseScrewPillarBracket002"
  Base = -> Sketch020
  Dir = (0,0,1)
  DirMode = 2
  FaceMakerClass = Part::FaceMakerBullseye
  LengthFwd = 2.4
  LengthRev = 0
  Placement = pos=(13.7,29,13.26) rot=(0,1,0;-1.5708rad)
  Solid = true
  Symmetric = false
FEATURE [Sketcher::SketchObject] Sketch021
  FullyConstrained = true
  sketch-geometry (7):
    g0: LineSegment StartX=0 StartY=0 StartZ=0 EndX=0 EndY=6 EndZ=0
    g1: Circle CenterX=0 CenterY=0 CenterZ=0 NormalX=0 NormalY=0 NormalZ=1 AngleXU=0 Radius=1
    g2: Circle CenterX=8 CenterY=6 CenterZ=0 NormalX=0 NormalY=0 NormalZ=1 AngleXU=0 Radius=1
    g3: BSplineCurve PolesCount=3 KnotsCount=2 Degree=2 IsPeriodic=0
    g4: GeomPoint X=0 Y=0 Z=0
    g5: GeomPoint X=8 Y=6 Z=0
    g6: LineSegment StartX=0 StartY=6 StartZ=0 EndX=8 EndY=6 EndZ=0
  constraints (14):
    c: Coincident(g0,g-1)
    c: Distance(g0) = 6
    c: Vertical(g0)
    c: Coincident(g3,g0)
    c: Weight(g1) = 1
    c: Equal(g1,g2)
    c: InternalAlignment(g1,g3)
    c: InternalAlignment(g2,g3)
    c: InternalAlignment(g4,g3)
    c: InternalAlignment(g5,g3)
    c: Block(g3)
    c: Coincident(g6,g0)
    c: Coincident(g6,g3)
    c: Horizontal(g6)
FEATURE [Part::Extrusion] Extrude015  label="caseScrewPillarBracket003"
  Base = -> Sketch021
  Dir = (0,0,1)
  DirMode = 2
  FaceMakerClass = Part::FaceMakerBullseye
  LengthFwd = 2.4
  LengthRev = 0
  Placement = pos=(11.3,29,58.74) rot=(0,1,0;1.5708rad)
  Solid = true
  Symmetric = false
FEATURE [Sketcher::SketchObject] Sketch022
  FullyConstrained = true
  sketch-geometry (7):
    g0: LineSegment StartX=0 StartY=0 StartZ=0 EndX=0 EndY=6 EndZ=0
    g1: Circle CenterX=0 CenterY=0 CenterZ=0 NormalX=0 NormalY=0 NormalZ=1 AngleXU=0 Radius=1
    g2: Circle CenterX=8 CenterY=6 CenterZ=0 NormalX=0 NormalY=0 NormalZ=1 AngleXU=0 Radius=1
    g3: BSplineCurve PolesCount=3 KnotsCount=2 Degree=2 IsPeriodic=0
    g4: GeomPoint X=0 Y=0 Z=0
    g5: GeomPoint X=8 Y=6 Z=0
    g6: LineSegment StartX=0 StartY=6 StartZ=0 EndX=8 EndY=6 EndZ=0
  constraints (14):
    c: Coincident(g0,g-1)
    c: Distance(g0) = 6
    c: Vertical(g0)
    c: Coincident(g3,g0)
    c: Weight(g1) = 1
    c: Equal(g1,g2)
    c: InternalAlignment(g1,g3)
    c: InternalAlignment(g2,g3)
    c: InternalAlignment(g4,g3)
    c: InternalAlignment(g5,g3)
    c: Block(g3)
    c: Coincident(g6,g0)
    c: Coincident(g6,g3)
    c: Horizontal(g6)
FEATURE [Part::Extrusion] Extrude016  label="caseScrewPillarBracket004"
  Base = -> Sketch022
  Dir = (0,0,1)
  DirMode = 2
  FaceMakerClass = Part::FaceMakerBullseye
  LengthFwd = 2.4
  LengthRev = 0
  Placement = pos=(88.3,29,65.23) rot=(0,1,0;1.5708rad)
  Solid = true
  Symmetric = false
FEATURE [Sketcher::SketchObject] Sketch023
  FullyConstrained = true
  sketch-geometry (7):
    g0: LineSegment StartX=0 StartY=0 StartZ=0 EndX=0 EndY=6 EndZ=0
    g1: Circle CenterX=0 CenterY=0 CenterZ=0 NormalX=0 NormalY=0 NormalZ=1 AngleXU=0 Radius=1
    g2: Circle CenterX=8 CenterY=6 CenterZ=0 NormalX=0 NormalY=0 NormalZ=1 AngleXU=0 Radius=1
    g3: BSplineCurve PolesCount=3 KnotsCount=2 Degree=2 IsPeriodic=0
    g4: GeomPoint X=0 Y=0 Z=0
    g5: GeomPoint X=8 Y=6 Z=0
    g6: LineSegment StartX=0 StartY=6 StartZ=0 EndX=8 EndY=6 EndZ=0
  constraints (14):
    c: Coincident(g0,g-1)
    c: Distance(g0) = 6
    c: Vertical(g0)
    c: Coincident(g3,g0)
    c: Weight(g1) = 1
    c: Equal(g1,g2)
    c: InternalAlignment(g1,g3)
    c: InternalAlignment(g2,g3)
    c: InternalAlignment(g4,g3)
    c: InternalAlignment(g5,g3)
    c: Block(g3)
    c: Coincident(g6,g0)
    c: Coincident(g6,g3)
    c: Horizontal(g6)
FEATURE [Part::Extrusion] Extrude017  label="caseScrewPillarBracket005"
  Base = -> Sketch023
  Dir = (0,0,1)
  DirMode = 2
  FaceMakerClass = Part::FaceMakerBullseye
  LengthFwd = 2.4
  LengthRev = 0
  Placement = pos=(90.7,29,6.77) rot=(0,-1,0;1.5708rad)
  Solid = true
  Symmetric = false
FEATURE [Sketcher::SketchObject] Sketch024
  FullyConstrained = true
  sketch-geometry (7):
    g0: LineSegment StartX=0 StartY=0 StartZ=0 EndX=0 EndY=6 EndZ=0
    g1: Circle CenterX=0 CenterY=0 CenterZ=0 NormalX=0 NormalY=0 NormalZ=1 AngleXU=0 Radius=1
    g2: Circle CenterX=8 CenterY=6 CenterZ=0 NormalX=0 NormalY=0 NormalZ=1 AngleXU=0 Radius=1
    g3: BSplineCurve PolesCount=3 KnotsCount=2 Degree=2 IsPeriodic=0
    g4: GeomPoint X=0 Y=0 Z=0
    g5: GeomPoint X=8 Y=6 Z=0
    g6: LineSegment StartX=0 StartY=6 StartZ=0 EndX=8 EndY=6 EndZ=0
  constraints (14):
    c: Coincident(g0,g-1)
    c: Distance(g0) = 6
    c: Vertical(g0)
    c: Coincident(g3,g0)
    c: Weight(g1) = 1
    c: Equal(g1,g2)
    c: InternalAlignment(g1,g3)
    c: InternalAlignment(g2,g3)
    c: InternalAlignment(g4,g3)
    c: InternalAlignment(g5,g3)
    c: Block(g3)
    c: Coincident(g6,g0)
    c: Coincident(g6,g3)
    c: Horizontal(g6)
FEATURE [Part::Extrusion] Extrude018  label="caseScrewPillarBracket006"
  Base = -> Sketch024
  Dir = (0,0,1)
  DirMode = 2
  FaceMakerClass = Part::FaceMakerBullseye
  LengthFwd = 2.4
  LengthRev = 0
  Placement = pos=(103.7,29,6.77) rot=(0,-1,0;1.5708rad)
  Solid = true
  Symmetric = false
FEATURE [Sketcher::SketchObject] Sketch025
  FullyConstrained = true
  sketch-geometry (7):
    g0: LineSegment StartX=0 StartY=0 StartZ=0 EndX=0 EndY=6 EndZ=0
    g1: Circle CenterX=0 CenterY=0 CenterZ=0 NormalX=0 NormalY=0 NormalZ=1 AngleXU=0 Radius=1
    g2: Circle CenterX=8 CenterY=6 CenterZ=0 NormalX=0 NormalY=0 NormalZ=1 AngleXU=0 Radius=1
    g3: BSplineCurve PolesCount=3 KnotsCount=2 Degree=2 IsPeriodic=0
    g4: GeomPoint X=0 Y=0 Z=0
    g5: GeomPoint X=8 Y=6 Z=0
    g6: LineSegment StartX=0 StartY=6 StartZ=0 EndX=8 EndY=6 EndZ=0
  constraints (14):
    c: Coincident(g0,g-1)
    c: Distance(g0) = 6
    c: Vertical(g0)
    c: Coincident(g3,g0)
    c: Weight(g1) = 1
    c: Equal(g1,g2)
    c: InternalAlignment(g1,g3)
    c: InternalAlignment(g2,g3)
    c: InternalAlignment(g4,g3)
    c: InternalAlignment(g5,g3)
    c: Block(g3)
    c: Coincident(g6,g0)
    c: Coincident(g6,g3)
    c: Horizontal(g6)
FEATURE [Part::Extrusion] Extrude019  label="caseScrewPillarBracket007"
  Base = -> Sketch025
  Dir = (0,0,1)
  DirMode = 2
  FaceMakerClass = Part::FaceMakerBullseye
  LengthFwd = 2.4
  LengthRev = 0
  Placement = pos=(101.3,29,65.23) rot=(0,1,0;1.5708rad)
  Solid = true
  Symmetric = false
FEATURE [Part::Box] Box011  label="frontCaseScrewPillarBracket"
  AttacherType = Attacher::AttachEngine3D
  Height = 2.4
  Length = 16
  Placement = pos=(87,28,2.3) rot=(0,0,1;0rad)
  Width = 7
FEATURE [Part::Box] Box012  label="frontCaseScrewPillarBracket001"
  AttacherType = Attacher::AttachEngine3D
  Height = 2.4
  Length = 16
  Placement = pos=(87,28,67.3) rot=(0,0,1;0rad)
  Width = 7
FEATURE [Sketcher::SketchObject] Sketch026
  FullyConstrained = true
  sketch-geometry (17):
    g0: Circle CenterX=-3.5 CenterY=23.5 CenterZ=0 NormalX=0 NormalY=0 NormalZ=1 AngleXU=0 Radius=1
    g1: Circle CenterX=-1 CenterY=15.25 CenterZ=0 NormalX=0 NormalY=0 NormalZ=1 AngleXU=0 Radius=1
    g2: Circle CenterX=-3.5 CenterY=7 CenterZ=0 NormalX=0 NormalY=0 NormalZ=1 AngleXU=0 Radius=1
    g3: BSplineCurve PolesCount=3 KnotsCount=2 Degree=2 IsPeriodic=0
    g4: GeomPoint X=-3.5 Y=23.5 Z=0
    g5: GeomPoint X=-3.5 Y=7 Z=0
    g6: Circle CenterX=-4.8 CenterY=30.5 CenterZ=0 NormalX=0 NormalY=0 NormalZ=1 AngleXU=0 Radius=1
    g7: Circle CenterX=-3.5 CenterY=30.5 CenterZ=0 NormalX=0 NormalY=0 NormalZ=1 AngleXU=0 Radius=1
    g8: Circle CenterX=-3.5 CenterY=29.2 CenterZ=0 NormalX=0 NormalY=0 NormalZ=1 AngleXU=0 Radius=1
    g9: BSplineCurve PolesCount=3 KnotsCount=2 Degree=2 IsPeriodic=0
    g10: GeomPoint X=-4.8 Y=30.5 Z=0
    g11: GeomPoint X=-3.5 Y=29.2 Z=0
    g12: LineSegment StartX=-3.5 StartY=29.2 StartZ=0 EndX=-3.5 EndY=23.5 EndZ=0
    g13: LineSegment StartX=-4.8 StartY=30.5 StartZ=0 EndX=0 EndY=30.5 EndZ=0
    g14: LineSegment StartX=-3.5 StartY=5 StartZ=0 EndX=-3.5 EndY=7 EndZ=0
    g15: LineSegment StartX=0 StartY=5 StartZ=0 EndX=0 EndY=30.5 EndZ=0
    g16: LineSegment StartX=-3.5 StartY=5 StartZ=0 EndX=0 EndY=5 EndZ=0
  constraints (33):
    c: Weight(g0) = 1
    c: Equal(g0,g1)
    c: Equal(g0,g2)
    c: InternalAlignment(g0,g3)
    c: InternalAlignment(g1,g3)
    c: InternalAlignment(g2,g3)
    c: InternalAlignment(g4,g3)
    c: InternalAlignment(g5,g3)
    c: Block(g3)
    c: Weight(g6) = 1
    c: Equal(g6,g7)
    c: Equal(g6,g8)
    c: InternalAlignment(g6,g9)
    c: InternalAlignment(g7,g9)
    c: InternalAlignment(g8,g9)
    c: InternalAlignment(g10,g9)
    c: InternalAlignment(g11,g9)
    c: Block(g9)
    c: Coincident(g12,g9)
    c: Coincident(g12,g3)
    c: Vertical(g12)
    c: Coincident(g13,g9)
    c: Horizontal(g13)
    c: Distance(g13) = 4.8
    c: Coincident(g14,g3)
    c: Vertical(g14)
    c: Coincident(g15,g13)
    c: Vertical(g15)
    c: Tangent(g15,g1)
    c: Distance(g14) = 2
    c: Coincident(g16,g14)
    c: Horizontal(g16)
    c: Coincident(g15,g16)
FEATURE [Part::Feature] Face050
  shape: bbox 4.8 x 25.5 x 2e-07 mm, 1 faces, 0 solids (baked)
FEATURE [Part::Revolution] Revolve054  label="moreFrontCaseScrewPost001"
  Angle = 360
  Axis = (0,1,0)
  Base = (0,0,0)
  FaceMakerClass = Part::FaceMakerBullseye
  Placement = pos=(102.5,4.5,3.5) rot=(0,0,1;0rad)
  Solid = false
  Source = -> Face050
  Symmetric = false
FEATURE [Part::Feature] Face051
  shape: bbox 4.8 x 25.5 x 2e-07 mm, 1 faces, 0 solids (baked)
FEATURE [Part::Revolution] Revolve055  label="moreFrontCaseScrewPost002"
  Angle = 360
  Axis = (0,1,0)
  Base = (0,0,0)
  FaceMakerClass = Part::FaceMakerBullseye
  Placement = pos=(102.5,4.5,68.5) rot=(0,0,1;0rad)
  Solid = false
  Source = -> Face051
  Symmetric = false
FEATURE [Sketcher::SketchObject] Sketch027
  FullyConstrained = true
  sketch-geometry (10):
    g0: LineSegment StartX=-1.6 StartY=4.7 StartZ=0 EndX=-1.6 EndY=1.7 EndZ=0
    g1: LineSegment StartX=-3.5 StartY=4.7 StartZ=0 EndX=-1.6 EndY=4.7 EndZ=0
    g2: LineSegment StartX=-1.6 StartY=1.7 StartZ=0 EndX=-1.6 EndY=1.5 EndZ=0
    g3: LineSegment StartX=-1.6 StartY=1.5 StartZ=0 EndX=-5.2 EndY=1.5 EndZ=0
    g4: Circle CenterX=-3.5 CenterY=4.7 CenterZ=0 NormalX=0 NormalY=0 NormalZ=1 AngleXU=0 Radius=1
    g5: Circle CenterX=-3.59627 CenterY=2.99743 CenterZ=0 NormalX=0 NormalY=0 NormalZ=1 AngleXU=0 Radius=1
    g6: Circle CenterX=-5.2 CenterY=1.5 CenterZ=0 NormalX=0 NormalY=0 NormalZ=1 AngleXU=0 Radius=1
    g7: BSplineCurve PolesCount=3 KnotsCount=2 Degree=2 IsPeriodic=0
    g8: GeomPoint X=-3.5 Y=4.7 Z=0
    g9: GeomPoint X=-5.2 Y=1.5 Z=0
  constraints (23):
    c: Vertical(g0)
    c: Distance(g0) = 3
    c: Coincident(g1,g0)
    c: Horizontal(g1)
    c: Block(g0)
    c: Block(g1)
    c: Coincident(g2,g0)
    c: Vertical(g2)
    c: Distance(g2) = 0.2
    c: Coincident(g3,g2)
    c: Horizontal(g3)
    c: Block(g3)
    c: Coincident(g7,g1)
    c: Weight(g4) = 1
    c: Equal(g4,g5)
    c: Equal(g4,g6)
    c: Coincident(g7,g3)
    c: InternalAlignment(g4,g7)
    c: InternalAlignment(g5,g7)
    c: InternalAlignment(g6,g7)
    c: InternalAlignment(g8,g7)
    c: InternalAlignment(g9,g7)
    c: Block(g7)
FEATURE [Sketcher::SketchObject] Sketch028
  FullyConstrained = true
  sketch-geometry (18):
    g0: LineSegment StartX=0 StartY=3e-16 StartZ=0 EndX=0 EndY=1.7 EndZ=0
    g1: LineSegment StartX=-3.5 StartY=0 StartZ=0 EndX=-3.5 EndY=0.9 EndZ=0
    g2: Circle CenterX=-2.7 CenterY=1.7 CenterZ=0 NormalX=0 NormalY=0 NormalZ=1 AngleXU=0 Radius=1
    g3: Circle CenterX=-3.5 CenterY=1.7 CenterZ=0 NormalX=0 NormalY=0 NormalZ=1 AngleXU=0 Radius=1
    g4: Circle CenterX=-3.5 CenterY=0.9 CenterZ=0 NormalX=0 NormalY=0 NormalZ=1 AngleXU=0 Radius=1
    g5: BSplineCurve PolesCount=3 KnotsCount=2 Degree=2 IsPeriodic=0
    g6: GeomPoint X=-2.7 Y=1.7 Z=0
    g7: GeomPoint X=-3.5 Y=0.9 Z=0
    g8: LineSegment StartX=-3.5 StartY=0 StartZ=0 EndX=-3.5 EndY=-7 EndZ=0
    g9: LineSegment StartX=0 StartY=3e-16 StartZ=0 EndX=0 EndY=-7 EndZ=0
    g10: LineSegment StartX=-3.5 StartY=-7 StartZ=0 EndX=0 EndY=-7 EndZ=0
    g11: LineSegment StartX=-2.7 StartY=1.7 StartZ=0 EndX=-1.6 EndY=1.7 EndZ=0
    g12: LineSegment StartX=0 StartY=1.7 StartZ=0 EndX=0 EndY=4.5 EndZ=0
    g13: LineSegment StartX=0 StartY=4.5 StartZ=0 EndX=0 EndY=10.8 EndZ=0
    g14: LineSegment StartX=0 StartY=10.8 StartZ=0 EndX=-2 EndY=10.8 EndZ=0
    g15: LineSegment StartX=-1.6 StartY=4.7 StartZ=0 EndX=-1.6 EndY=1.7 EndZ=0
    g16: LineSegment StartX=-1.6 StartY=4.7 StartZ=0 EndX=-2 EndY=4.7 EndZ=0
    g17: LineSegment StartX=-2 StartY=4.7 StartZ=0 EndX=-2 EndY=10.8 EndZ=0
  constraints (44):
    c: Vertical(g0)
    c: Vertical(g1)
    c: Distance(g1) = 0.9
    c: Block(g0)
    c: Distance(g0) = 1.7
    c: Weight(g2) = 1
    c: Equal(g2,g3)
    c: Equal(g2,g4)
    c: Coincident(g5,g1)
    c: InternalAlignment(g2,g5)
    c: InternalAlignment(g3,g5)
    c: InternalAlignment(g4,g5)
    c: InternalAlignment(g6,g5)
    c: InternalAlignment(g7,g5)
    c: Block(g5)
    c: Coincident(g8,g1)
    c: Vertical(g8)
    c: Distance(g8) = 7
    c: Vertical(g9)
    c: Equal(g8,g9) = 7
    c: Coincident(g9,g0)
    c: Coincident(g10,g8)
    c: Coincident(g10,g9)
    c: Horizontal(g10)
    c: Coincident(g11,g5)
    c: Horizontal(g11)
    c: Coincident(g12,g0)
    c: Vertical(g12)
    c: Distance(g12) = 2.8
    c: Coincident(g13,g12)
    c: Vertical(g13)
    c: Distance(g13) = 6.3
    c: Coincident(g14,g13)
    c: Horizontal(g14)
    c: Distance(g14) = 2
    c: Vertical(g15)
    c: Distance(g15) = 3
    c: Block(g11)
    c: Coincident(g15,g11)
    c: Coincident(g16,g15)
    c: Horizontal(g16)
    c: Coincident(g17,g16)
    c: Coincident(g17,g14)
    c: Vertical(g17)
FEATURE [Part::Revolution] Revolve040  label="backCaseScrewRetainer001"
  Angle = 360
  Axis = (0,1,0)
  Base = (0,0,0)
  FaceMakerClass = Part::FaceMakerBullseye
  Placement = pos=(12.5,3,10) rot=(0,0,1;0rad)
  Solid = false
  Source = -> Face036
  Symmetric = false
FEATURE [Part::Feature] Face055
  shape: bbox 3.5 x 30.2 x 2e-07 mm, 1 faces, 0 solids (baked)
FEATURE [Part::Revolution] Revolve059  label="backCaseScrewPost"
  Angle = 360
  Axis = (0,1,0)
  Base = (0,0,0)
  FaceMakerClass = Part::FaceMakerBullseye
  Placement = pos=(12.5,4.5,10) rot=(0,0,1;0rad)
  Solid = false
  Source = -> Face055
  Symmetric = false
FEATURE [Part::Feature] Face056
  shape: bbox 3.5 x 30.2 x 2e-07 mm, 1 faces, 0 solids (baked)
FEATURE [Part::Revolution] Revolve060  label="backCaseScrewPost001"
  Angle = 360
  Axis = (0,1,0)
  Base = (0,0,0)
  FaceMakerClass = Part::FaceMakerBullseye
  Placement = pos=(12.5,4.5,62) rot=(0,0,1;0rad)
  Solid = false
  Source = -> Face056
  Symmetric = false
FEATURE [Part::Feature] Face057
  shape: bbox 3.5 x 17.8 x 2e-07 mm, 1 faces, 0 solids (baked)
FEATURE [Part::Revolution] Revolve061  label="removeToCreateScrewAndThreadedInsertHole"
  Angle = 360
  Axis = (0,1,0)
  Base = (0,0,0)
  FaceMakerClass = Part::FaceMakerBullseye
  Placement = pos=(12.5,0,10) rot=(0,0,1;0rad)
  Solid = false
  Source = -> Face057
  Symmetric = false
FEATURE [Part::Feature] Face058
  shape: bbox 3.5 x 17.8 x 2e-07 mm, 1 faces, 0 solids (baked)
FEATURE [Part::Revolution] Revolve062  label="removeToCreateScrewAndThreadedInsertHole001"
  Angle = 360
  Axis = (0,1,0)
  Base = (0,0,0)
  FaceMakerClass = Part::FaceMakerBullseye
  Placement = pos=(12.5,0,62) rot=(0,0,1;0rad)
  Solid = false
  Source = -> Face058
  Symmetric = false
FEATURE [Part::Feature] Face059
  shape: bbox 3.5 x 17.8 x 2e-07 mm, 1 faces, 0 solids (baked)
FEATURE [Part::Revolution] Revolve063  label="removeToCreateScrewAndThreadedInsertHole002"
  Angle = 360
  Axis = (0,1,0)
  Base = (0,0,0)
  FaceMakerClass = Part::FaceMakerBullseye
  Placement = pos=(89.5,0,68.5) rot=(0,0,1;0rad)
  Solid = false
  Source = -> Face059
  Symmetric = false
FEATURE [Part::Feature] Face060
  shape: bbox 3.5 x 17.8 x 2e-07 mm, 1 faces, 0 solids (baked)
FEATURE [Part::Revolution] Revolve064  label="removeToCreateScrewAndThreadedInsertHole003"
  Angle = 360
  Axis = (0,1,0)
  Base = (0,0,0)
  FaceMakerClass = Part::FaceMakerBullseye
  Placement = pos=(89.5,0,3.5) rot=(0,0,1;0rad)
  Solid = false
  Source = -> Face060
  Symmetric = false
FEATURE [Part::Feature] Face061
  shape: bbox 3.5 x 17.8 x 2e-07 mm, 1 faces, 0 solids (baked)
FEATURE [Part::Revolution] Revolve065  label="removeToCreateScrewAndThreadedInsertHole004"
  Angle = 360
  Axis = (0,1,0)
  Base = (0,0,0)
  FaceMakerClass = Part::FaceMakerBullseye
  Placement = pos=(102.5,4.7,3.5) rot=(0,0,1;0rad)
  Solid = false
  Source = -> Face061
  Symmetric = false
FEATURE [Part::Feature] Face062
  shape: bbox 3.5 x 17.8 x 2e-07 mm, 1 faces, 0 solids (baked)
FEATURE [Part::Revolution] Revolve066  label="removeToCreateScrewAndThreadedInsertHole005"
  Angle = 360
  Axis = (0,1,0)
  Base = (0,0,0)
  FaceMakerClass = Part::FaceMakerBullseye
  Placement = pos=(102.5,4.7,68.5) rot=(0,0,1;0rad)
  Solid = false
  Source = -> Face062
  Symmetric = false
FEATURE [Part::MultiFuse] Fusion047  label="makeHoles"
  Shapes = -> [Revolve066,Revolve065,Revolve064,Revolve063,Revolve062,Revolve061]
FEATURE [Part::Feature] Face063
  shape: bbox 3.6 x 3.2 x 2e-07 mm, 1 faces, 0 solids (baked)
FEATURE [Part::Revolution] Revolve067  label="moreFrontCaseScrewRetainer002"
  Angle = 360
  Axis = (0,1,0)
  Base = (0,0,0)
  FaceMakerClass = Part::FaceMakerBullseye
  Placement = pos=(102.5,4.5,68.5) rot=(0,0,1;0rad)
  Solid = false
  Source = -> Face063
  Symmetric = false
FEATURE [Part::Feature] Face064
  shape: bbox 3.6 x 3.2 x 2e-07 mm, 1 faces, 0 solids (baked)
FEATURE [Part::Revolution] Revolve068  label="moreFrontCaseScrewRetainer003"
  Angle = 360
  Axis = (0,1,0)
  Base = (0,0,0)
  FaceMakerClass = Part::FaceMakerBullseye
  Placement = pos=(102.5,4.5,3.5) rot=(0,0,1;0rad)
  Solid = false
  Source = -> Face064
  Symmetric = false
FEATURE [Part::Cut] Cut014  label="bottom003"
  Base = -> Cut007
  Tool = -> Fusion047
FEATURE [Part::Feature] Face065
  shape: bbox 3.5 x 17.8 x 2e-07 mm, 1 faces, 0 solids (baked)
FEATURE [Part::Revolution] Revolve069  label="removeToCreateScrewAndThreadedInsertHole006"
  Angle = 360
  Axis = (0,1,0)
  Base = (0,0,0)
  FaceMakerClass = Part::FaceMakerBullseye
  Placement = pos=(12.5,0,10) rot=(0,0,1;0rad)
  Solid = false
  Source = -> Face065
  Symmetric = false
FEATURE [Part::Feature] Face066
  shape: bbox 3.5 x 17.8 x 2e-07 mm, 1 faces, 0 solids (baked)
FEATURE [Part::Revolution] Revolve070  label="removeToCreateScrewAndThreadedInsertHole007"
  Angle = 360
  Axis = (0,1,0)
  Base = (0,0,0)
  FaceMakerClass = Part::FaceMakerBullseye
  Placement = pos=(12.5,0,62) rot=(0,0,1;0rad)
  Solid = false
  Source = -> Face066
  Symmetric = false
FEATURE [Part::Feature] Face067
  shape: bbox 3.5 x 17.8 x 2e-07 mm, 1 faces, 0 solids (baked)
FEATURE [Part::Revolution] Revolve071  label="removeToCreateScrewAndThreadedInsertHole008"
  Angle = 360
  Axis = (0,1,0)
  Base = (0,0,0)
  FaceMakerClass = Part::FaceMakerBullseye
  Placement = pos=(89.5,0,68.5) rot=(0,0,1;0rad)
  Solid = false
  Source = -> Face067
  Symmetric = false
FEATURE [Part::Feature] Face068
  shape: bbox 3.5 x 17.8 x 2e-07 mm, 1 faces, 0 solids (baked)
FEATURE [Part::Revolution] Revolve072  label="removeToCreateScrewAndThreadedInsertHole009"
  Angle = 360
  Axis = (0,1,0)
  Base = (0,0,0)
  FaceMakerClass = Part::FaceMakerBullseye
  Placement = pos=(89.5,0,3.5) rot=(0,0,1;0rad)
  Solid = false
  Source = -> Face068
  Symmetric = false
FEATURE [Part::Feature] Face069
  shape: bbox 3.5 x 17.8 x 2e-07 mm, 1 faces, 0 solids (baked)
FEATURE [Part::Feature] Face070
  shape: bbox 3.5 x 17.8 x 2e-07 mm, 1 faces, 0 solids (baked)
FEATURE [Part::Revolution] Revolve073  label="removeToCreateScrewAndThreadedInsertHole010"
  Angle = 360
  Axis = (0,1,0)
  Base = (0,0,0)
  FaceMakerClass = Part::FaceMakerBullseye
  Placement = pos=(102.5,4.7,3.5) rot=(0,0,1;0rad)
  Solid = false
  Source = -> Face069
  Symmetric = false
FEATURE [Part::Revolution] Revolve074  label="removeToCreateScrewAndThreadedInsertHole011"
  Angle = 360
  Axis = (0,1,0)
  Base = (0,0,0)
  FaceMakerClass = Part::FaceMakerBullseye
  Placement = pos=(102.5,4.7,68.5) rot=(0,0,1;0rad)
  Solid = false
  Source = -> Face070
  Symmetric = false
FEATURE [Part::MultiFuse] Fusion048  label="makeHoles001"
  Shapes = -> [Revolve074,Revolve073,Revolve072,Revolve071,Revolve070,Revolve069]
FEATURE [Part::MultiFuse] Fusion049  label="caseScrewRetainers"
  Shapes = -> [Revolve067,Revolve068,Revolve048,Revolve047,Revolve039,Revolve040]
FEATURE [Part::Cut] Cut015  label="caseScrewRetainers001"
  Base = -> Fusion049
  Tool = -> Fusion048
FEATURE [Part::MultiFuse] Fusion050  label="casePillars"
  Shapes = -> [Revolve055,Revolve054,Revolve043,Revolve046,Revolve059,Revolve060]
FEATURE [Part::Feature] Face071 .. Face076  x6 (patterned run collapsed; names and placements below)
  shape: bbox 3.5 x 17.8 x 2e-07 mm, 1 faces, 0 solids (baked)
FEATURE [Part::Revolution] Revolve075  label="removeToCreateScrewAndThreadedInsertHole012"
  Angle = 360
  Axis = (0,1,0)
  Base = (0,0,0)
  FaceMakerClass = Part::FaceMakerBullseye
  Placement = pos=(12.5,0,10) rot=(0,0,1;0rad)
  Solid = false
  Source = -> Face071
  Symmetric = false
FEATURE [Part::Revolution] Revolve076  label="removeToCreateScrewAndThreadedInsertHole013"
  Angle = 360
  Axis = (0,1,0)
  Base = (0,0,0)
  FaceMakerClass = Part::FaceMakerBullseye
  Placement = pos=(12.5,0,62) rot=(0,0,1;0rad)
  Solid = false
  Source = -> Face072
  Symmetric = false
FEATURE [Part::Revolution] Revolve077  label="removeToCreateScrewAndThreadedInsertHole014"
  Angle = 360
  Axis = (0,1,0)
  Base = (0,0,0)
  FaceMakerClass = Part::FaceMakerBullseye
  Placement = pos=(89.5,0,68.5) rot=(0,0,1;0rad)
  Solid = false
  Source = -> Face073
  Symmetric = false
FEATURE [Part::Revolution] Revolve078  label="removeToCreateScrewAndThreadedInsertHole015"
  Angle = 360
  Axis = (0,1,0)
  Base = (0,0,0)
  FaceMakerClass = Part::FaceMakerBullseye
  Placement = pos=(89.5,0,3.5) rot=(0,0,1;0rad)
  Solid = false
  Source = -> Face074
  Symmetric = false
FEATURE [Part::Revolution] Revolve079  label="removeToCreateScrewAndThreadedInsertHole016"
  Angle = 360
  Axis = (0,1,0)
  Base = (0,0,0)
  FaceMakerClass = Part::FaceMakerBullseye
  Placement = pos=(102.5,4.7,3.5) rot=(0,0,1;0rad)
  Solid = false
  Source = -> Face075
  Symmetric = false
FEATURE [Part::Revolution] Revolve080  label="removeToCreateScrewAndThreadedInsertHole017"
  Angle = 360
  Axis = (0,1,0)
  Base = (0,0,0)
  FaceMakerClass = Part::FaceMakerBullseye
  Placement = pos=(102.5,4.7,68.5) rot=(0,0,1;0rad)
  Solid = false
  Source = -> Face076
  Symmetric = false
FEATURE [Part::MultiFuse] Fusion051  label="makeHoles002"
  Shapes = -> [Revolve080,Revolve079,Revolve078,Revolve077,Revolve076,Revolve075]
FEATURE [Part::Cut] Cut016  label="caesPillars"
  Base = -> Fusion050
  Tool = -> Fusion051
FEATURE [Part::Revolution] Revolve009  label="plugHousing016"
  Angle = 360
  Axis = (0,1,0)
  Base = (0,0,0)
  FaceMakerClass = Part::FaceMakerBullseye
  Placement = pos=(0,0,36.15) rot=(0,0,1;0rad)
  Solid = false
  Source = -> Face012
  Symmetric = false
FEATURE [Part::MultiFuse] Fusion014  label="plugHousing023"
  Placement = pos=(0,0,0) rot=(0,0,1;1.5708rad)
  Shapes = -> [Revolve011,Revolve009]
FEATURE [Part::Revolution] Revolve010  label="plugHousing017"
  Angle = 360
  Axis = (0,1,0)
  Base = (0,0,0)
  FaceMakerClass = Part::FaceMakerBullseye
  Placement = pos=(0,0,36.15) rot=(0,0,1;0rad)
  Solid = false
  Source = -> Face014
  Symmetric = false
FEATURE [Part::MultiFuse] Fusion015  label="plugHousing024"
  Placement = pos=(0,0,0) rot=(0,0,1;1.5708rad)
  Shapes = -> [Revolve010,Revolve015]
FEATURE [Part::Revolution] Revolve014  label="plugHousing026"
  Angle = 360
  Axis = (0,1,0)
  Base = (0,0,0)
  FaceMakerClass = Part::FaceMakerBullseye
  Placement = pos=(0,0,36.15) rot=(0,0,1;0rad)
  Solid = false
  Source = -> Face011
  Symmetric = false
FEATURE [Part::Revolution] Revolve013  label="plugHousing025"
  Angle = 360
  Axis = (0,1,0)
  Base = (0,0,0)
  FaceMakerClass = Part::FaceMakerBullseye
  Placement = pos=(0,0,36.15) rot=(0,0,1;0rad)
  Solid = false
  Source = -> Face015
  Symmetric = false
FEATURE [Part::MultiFuse] Fusion016  label="plugHousing028"
  Placement = pos=(0,19,0) rot=(0,0,1;3.14159rad)
  Shapes = -> [Fusion014,Fusion013]
FEATURE [Part::MultiFuse] Fusion011  label="plugHousing018"
  Placement = pos=(0,0,0) rot=(0,0,1;1.5708rad)
  Shapes = -> [Revolve014,Revolve013]
FEATURE [Part::MultiFuse] Fusion012  label="plugHousing019"
  Placement = pos=(0,19,0) rot=(0,0,1;3.14159rad)
  Shapes = -> [Fusion011,Fusion015]
FEATURE [Part::MultiFuse] Fusion017  label="plugHousing029"
  Placement = pos=(122.621,0,-0.15) rot=(0,0,1;0rad)
  Shapes = -> [Fusion016,Fusion012]
FEATURE [Part::MultiFuse] Fusion052  label="casePillarRetainers"
  Shapes = -> [Extrude012,Extrude013,Extrude014,Extrude015,Extrude016,Extrude017,Extrude018,Extrude019,Box011,Box012]
FEATURE [Part::Feature] Face077
  shape: bbox 3.5 x 17.8 x 2e-07 mm, 1 faces, 0 solids (baked)
FEATURE [Part::Revolution] Revolve081  label="removeToCreateScrewAndThreadedInsertHole018"
  Angle = 360
  Axis = (0,1,0)
  Base = (0,0,0)
  FaceMakerClass = Part::FaceMakerBullseye
  Placement = pos=(62.3,30.3,19.7) rot=(0,0,1;0rad)
  Solid = false
  Source = -> Face077
  Symmetric = false
FEATURE [Part::Feature] Face078
  shape: bbox 3.5 x 17.8 x 2e-07 mm, 1 faces, 0 solids (baked)
FEATURE [Part::Revolution] Revolve082  label="removeToCreateScrewAndThreadedInsertHole019"
  Angle = 360
  Axis = (0,1,0)
  Base = (0,0,0)
  FaceMakerClass = Part::FaceMakerBullseye
  Placement = pos=(62.3,30.3,51.7) rot=(0,0,1;0rad)
  Solid = false
  Source = -> Face078
  Symmetric = false
FEATURE [Part::Feature] Face079
  shape: bbox 3.5 x 17.8 x 2e-07 mm, 1 faces, 0 solids (baked)
FEATURE [Part::Revolution] Revolve083  label="removeToCreateScrewAndThreadedInsertHole020"
  Angle = 360
  Axis = (0,1,0)
  Base = (0,0,0)
  FaceMakerClass = Part::FaceMakerBullseye
  Placement = pos=(30.3,30.3,19.7) rot=(0,0,1;0rad)
  Solid = false
  Source = -> Face079
  Symmetric = false
FEATURE [Part::Feature] Face080
  shape: bbox 3.5 x 17.8 x 2e-07 mm, 1 faces, 0 solids (baked)
FEATURE [Part::Revolution] Revolve084  label="removeToCreateScrewAndThreadedInsertHole021"
  Angle = 360
  Axis = (0,1,0)
  Base = (0,0,0)
  FaceMakerClass = Part::FaceMakerBullseye
  Placement = pos=(30.3,30.3,51.7) rot=(0,0,1;0rad)
  Solid = false
  Source = -> Face080
  Symmetric = false
FEATURE [Part::MultiFuse] Fusion053  label="createThreadedInsertHolesForFan"
  Shapes = -> [Revolve081,Revolve082,Revolve083,Revolve084]
FEATURE [Part::Cut] Cut017  label="fanScrewHousing001"
  Base = -> Fusion046
  Tool = -> Fusion053
FEATURE [Part::Feature] Face081
  shape: bbox 3.5 x 17.8 x 2e-07 mm, 1 faces, 0 solids (baked)
FEATURE [Part::Revolution] Revolve085  label="removeToCreateScrewAndThreadedInsertHole022"
  Angle = 360
  Axis = (0,1,0)
  Base = (0,0,0)
  FaceMakerClass = Part::FaceMakerBullseye
  Placement = pos=(62.3,30.3,19.7) rot=(0,0,1;0rad)
  Solid = false
  Source = -> Face081
  Symmetric = false
FEATURE [Part::Feature] Face082
  shape: bbox 3.5 x 17.8 x 2e-07 mm, 1 faces, 0 solids (baked)
FEATURE [Part::Revolution] Revolve086  label="removeToCreateScrewAndThreadedInsertHole023"
  Angle = 360
  Axis = (0,1,0)
  Base = (0,0,0)
  FaceMakerClass = Part::FaceMakerBullseye
  Placement = pos=(62.3,30.3,51.7) rot=(0,0,1;0rad)
  Solid = false
  Source = -> Face082
  Symmetric = false
FEATURE [Part::Feature] Face083
  shape: bbox 3.5 x 17.8 x 2e-07 mm, 1 faces, 0 solids (baked)
FEATURE [Part::Revolution] Revolve087  label="removeToCreateScrewAndThreadedInsertHole024"
  Angle = 360
  Axis = (0,1,0)
  Base = (0,0,0)
  FaceMakerClass = Part::FaceMakerBullseye
  Placement = pos=(30.3,30.3,19.7) rot=(0,0,1;0rad)
  Solid = false
  Source = -> Face083
  Symmetric = false
FEATURE [Part::Feature] Face084
  shape: bbox 3.5 x 17.8 x 2e-07 mm, 1 faces, 0 solids (baked)
FEATURE [Part::Revolution] Revolve088  label="removeToCreateScrewAndThreadedInsertHole025"
  Angle = 360
  Axis = (0,1,0)
  Base = (0,0,0)
  FaceMakerClass = Part::FaceMakerBullseye
  Placement = pos=(30.3,30.3,51.7) rot=(0,0,1;0rad)
  Solid = false
  Source = -> Face084
  Symmetric = false
FEATURE [Part::MultiFuse] Fusion054  label="createThreadedInsertHolesForFan001"
  Shapes = -> [Revolve085,Revolve086,Revolve087,Revolve088]
FEATURE [Part::Cut] Cut018  label="top007"
  Base = -> Fusion040
  Tool = -> Fusion054
FEATURE [Sketcher::SketchObject] Sketch029
  FullyConstrained = false
  Placement = pos=(0,0,0) rot=(-1,0,0;4.71239rad)
  sketch-geometry (24):
    g0: ArcOfCircle CenterX=-4 CenterY=-10.5 CenterZ=0 NormalX=0 NormalY=0 NormalZ=1 AngleXU=0 Radius=1.5 StartAngle=6e-16 EndAngle=3.14159
    g1: ArcOfCircle CenterX=-34.2 CenterY=-10.5 CenterZ=0 NormalX=0 NormalY=0 NormalZ=1 AngleXU=0 Radius=1.5 StartAngle=0 EndAngle=3.14159
    g2: ArcOfCircle CenterX=-34.2 CenterY=-27.7 CenterZ=0 NormalX=0 NormalY=0 NormalZ=1 AngleXU=0 Radius=1.5 StartAngle=3.14159 EndAngle=6.28319
    g3: ArcOfCircle CenterX=-4 CenterY=-27.7 CenterZ=0 NormalX=0 NormalY=0 NormalZ=1 AngleXU=0 Radius=1.5 StartAngle=3.1416 EndAngle=6.28319
    g4: ArcOfCircle CenterX=-10 CenterY=-4.3 CenterZ=0 NormalX=0 NormalY=0 NormalZ=1 AngleXU=0 Radius=1.5 StartAngle=2e-16 EndAngle=3.14159
    g5: ArcOfCircle CenterX=-16.1 CenterY=-1.8 CenterZ=0 NormalX=0 NormalY=0 NormalZ=1 AngleXU=0 Radius=1.5 StartAngle=5e-16 EndAngle=3.14159
    g6: ArcOfCircle CenterX=-22.1 CenterY=-1.8 CenterZ=0 NormalX=0 NormalY=0 NormalZ=1 AngleXU=0 Radius=1.5 StartAngle=5e-16 EndAngle=3.14159
    g7: ArcOfCircle CenterX=-28.2 CenterY=-4.3 CenterZ=0 NormalX=0 NormalY=0 NormalZ=1 AngleXU=0 Radius=1.5 StartAngle=2e-16 EndAngle=3.14159
    g8: ArcOfCircle CenterX=-10 CenterY=-33.9 CenterZ=0 NormalX=0 NormalY=0 NormalZ=1 AngleXU=0 Radius=1.5 StartAngle=3.14159 EndAngle=6.28319
    g9: ArcOfCircle CenterX=-16.1 CenterY=-36.4 CenterZ=0 NormalX=0 NormalY=0 NormalZ=1 AngleXU=0 Radius=1.5 StartAngle=3.14159 EndAngle=6.28319
    g10: ArcOfCircle CenterX=-22.1 CenterY=-36.4 CenterZ=0 NormalX=0 NormalY=0 NormalZ=1 AngleXU=0 Radius=1.5 StartAngle=3.14159 EndAngle=6.28319
    g11: ArcOfCircle CenterX=-28.2 CenterY=-33.9 CenterZ=0 NormalX=0 NormalY=0 NormalZ=1 AngleXU=0 Radius=1.5 StartAngle=3.14159 EndAngle=6.28319
    g12: LineSegment StartX=-35.7 StartY=-10.5 StartZ=0 EndX=-35.7 EndY=-27.7 EndZ=0
    g13: LineSegment StartX=-32.7 StartY=-10.5 StartZ=0 EndX=-32.7 EndY=-27.7 EndZ=0
    g14: LineSegment StartX=-29.7 StartY=-33.9 StartZ=0 EndX=-29.7 EndY=-4.3 EndZ=0
    g15: LineSegment StartX=-26.7 StartY=-33.9 StartZ=0 EndX=-26.7 EndY=-4.3 EndZ=0
    g16: LineSegment StartX=-2.5 StartY=-10.5 StartZ=0 EndX=-2.5 EndY=-27.7 EndZ=0
    g17: LineSegment StartX=-8.5 StartY=-4.3 StartZ=0 EndX=-8.5 EndY=-33.9 EndZ=0
    g18: LineSegment StartX=-5.5 StartY=-10.5 StartZ=0 EndX=-5.5 EndY=-27.7 EndZ=0
    g19: LineSegment StartX=-11.5 StartY=-4.3 StartZ=0 EndX=-11.5 EndY=-33.9 EndZ=0
    g20: LineSegment StartX=-14.6 StartY=-1.8 StartZ=0 EndX=-14.6 EndY=-36.4 EndZ=0
    g21: LineSegment StartX=-17.6 StartY=-1.8 StartZ=0 EndX=-17.6 EndY=-36.4 EndZ=0
    g22: LineSegment StartX=-20.6 StartY=-36.4 StartZ=0 EndX=-20.6 EndY=-1.8 EndZ=0
    g23: LineSegment StartX=-23.6 StartY=-1.8 StartZ=0 EndX=-23.6 EndY=-36.4 EndZ=0
  constraints (48):
    c: Block(g0)
    c: Block(g1)
    c: Block(g2)
    c: Block(g3)
    c: Block(g4)
    c: Block(g5)
    c: Block(g6)
    c: Block(g7)
    c: Block(g8)
    c: Block(g9)
    c: Block(g10)
    c: Block(g11)
    c: Coincident(g12,g1)
    c: Coincident(g12,g2)
    c: Vertical(g12)
    c: Coincident(g13,g1)
    c: Coincident(g13,g2)
    c: Vertical(g13)
    c: Coincident(g14,g11)
    c: Coincident(g14,g7)
    c: Vertical(g14)
    c: Coincident(g15,g11)
    c: Coincident(g15,g7)
    c: Vertical(g15)
    c: Coincident(g16,g0)
    c: Coincident(g16,g3)
    c: Vertical(g16)
    c: Coincident(g17,g4)
    c: Coincident(g17,g8)
    c: Vertical(g17)
    c: Coincident(g18,g0)
    c: Coincident(g18,g3)
    c: Vertical(g18)
    c: Coincident(g19,g4)
    c: Coincident(g19,g8)
    c: Vertical(g19)
    c: Coincident(g20,g5)
    c: Coincident(g20,g9)
    c: Vertical(g20)
    c: Coincident(g21,g5)
    c: Coincident(g21,g9)
    c: Vertical(g21)
    c: Coincident(g22,g10)
    c: Coincident(g22,g6)
    c: Vertical(g22)
    c: Coincident(g23,g6)
    c: Coincident(g23,g10)
    c: Vertical(g23)
FEATURE [Part::Extrusion] Extrude020
  Base = -> Sketch029
  Dir = (0,-1,3e-16)
  DirMode = 2
  FaceMakerClass = Part::FaceMakerBullseye
  LengthFwd = 10
  LengthRev = 0
  Solid = true
  Symmetric = false
